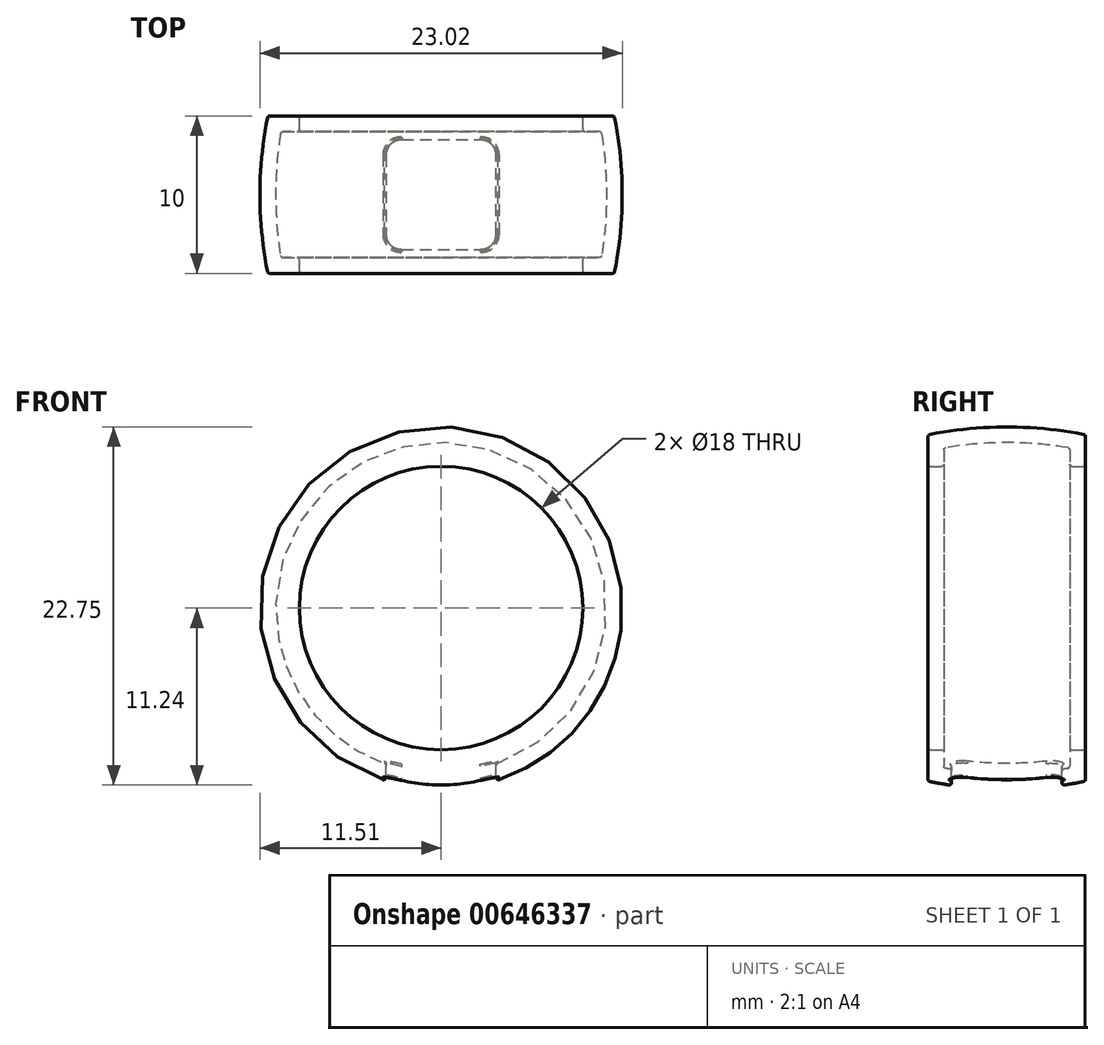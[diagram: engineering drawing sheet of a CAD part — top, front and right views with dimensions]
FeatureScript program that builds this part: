
annotation { "Feature Type Name" : "Feature", "Feature Type Description" : "" }
export const myFeature = defineFeature(function(context is Context, id is Id, definition is map)
    precondition{}
    {
        {
            var Q0;
            Q0=qCreatedBy(makeId("Top.planeOp"),FACE);
            var sketch = newSketch(context, id + "F0", { "sketchPlane" : qUnion([Q0])});
            skLineSegment(sketch, "E0", {"start": v(0, 0) * mm, "end": v(-9, 0) * mm, "construction": true});
            skLineSegment(sketch, "E1", {"start": v(-9, 5) * mm, "end": v(-9, -5) * mm});
            skLineSegment(sketch, "E2", {"start": v(-9, 5) * mm, "end": v(-11, 5) * mm});
            skLineSegment(sketch, "E3", {"start": v(-9, -5) * mm, "end": v(-11, -5) * mm});
            skArc(sketch, "E4", {"start": v(-11, 5) * mm, "mid": v(-11.5, 0) * mm, "end": v(-11, -5) * mm});
            skLineSegment(sketch, "E5", {"start": v(0, 0) * mm, "end": v(0, -13.53) * mm, "construction": true});
            skSolve(sketch);
        }
        {
            var Q0;
            Q0 = qSketchRegion(id + "F0", true);
            var Q1;
            Q1=sQuery(id+"F0.wireOp",EDGE,"E5");
            revolve(context, id + "F1", {"entities" : qUnion([Q0]), "axis" : qUnion([Q1]), "revolveType" : RevolveType.FULL});
        }
        {
            var Q0;
            Q0=makeQuery(id+"F1.opRevolve","SWEPT_FACE",FACE,{"disambiguationData":[OSD([sQuery(id+"F0.wireOp",EDGE,"E1")])]});
            shell(context, id + "F2", {"entities" : qUnion([Q0]), "thickness" : 1 * mm});
        }
        {
            var Q0;
            Q0=makeQuery(id+"F1.opRevolve","SWEPT_FACE",FACE,{"disambiguationData":[OSD([sQuery(id+"F0.wireOp",EDGE,"E4")])]});
            var Q1;
            Q1=makeQuery(id+"F1.opRevolve","SWEPT_EDGE",EDGE,{"disambiguationData":[OSD([sQuery(id+"F0.wireOp",EDGE,"E3"),sQuery(id+"F0.wireOp",EDGE,"E4")])]});
            var Q2;
            Q2=makeQuery(id+"F1.opRevolve","SWEPT_FACE",FACE,{"disambiguationData":[OSD([sQuery(id+"F0.wireOp",EDGE,"E3")])]});
            var Q3;
            Q3=makeQuery(id+"F1.opRevolve","SWEPT_EDGE",EDGE,{"disambiguationData":[OSD([sQuery(id+"F0.wireOp",EDGE,"E2"),sQuery(id+"F0.wireOp",EDGE,"E4")])]});
            var Q4;
            Q4=makeQuery(id+"F1.opRevolve","SWEPT_FACE",FACE,{"disambiguationData":[OSD([sQuery(id+"F0.wireOp",EDGE,"E2")])]});
            var Q5;
            Q5=makeQuery(id+"F1.opRevolve","SWEPT_EDGE",EDGE,{"disambiguationData":[OSD([sQuery(id+"F0.wireOp",EDGE,"E1"),sQuery(id+"F0.wireOp",EDGE,"E3")])]});
            var Q6;
            Q6=makeQuery(id+"F2.opShell","OFFSET_EDGE",EDGE,{"disambiguationData":[OSD([sQuery(id+"F0.wireOp",EDGE,"E1"),sQuery(id+"F0.wireOp",EDGE,"E2")])]});
            var Q7;
            Q7=makeQuery(id+"F1.opRevolve","SWEPT_EDGE",EDGE,{"disambiguationData":[OSD([sQuery(id+"F0.wireOp",EDGE,"E1"),sQuery(id+"F0.wireOp",EDGE,"E2")])]});
            var Q8;
            Q8=makeQuery(id+"F2.opShell","OFFSET_FACE",FACE,{"disambiguationData":[OSD([sQuery(id+"F0.wireOp",EDGE,"E1")])]});
            var Q9;
            Q9=makeQuery(id+"F2.opShell","OFFSET_EDGE",EDGE,{"disambiguationData":[OSD([sQuery(id+"F0.wireOp",EDGE,"E1"),sQuery(id+"F0.wireOp",EDGE,"E3")])]});
            var Q10;
            Q10=makeQuery(id+"F2.opShell","OFFSET_FACE",FACE,{"disambiguationData":[OSD([sQuery(id+"F0.wireOp",EDGE,"E2")])]});
            var Q11;
            Q11=makeQuery(id+"F2.opShell","OFFSET_EDGE",EDGE,{"disambiguationData":[OSD([sQuery(id+"F0.wireOp",EDGE,"E2"),sQuery(id+"F0.wireOp",EDGE,"E4")])]});
            var Q12;
            Q12=makeQuery(id+"F2.opShell","OFFSET_FACE",FACE,{"disambiguationData":[OSD([sQuery(id+"F0.wireOp",EDGE,"E3")])]});
            var Q13;
            Q13=makeQuery(id+"F2.opShell","OFFSET_FACE",FACE,{"disambiguationData":[OSD([sQuery(id+"F0.wireOp",EDGE,"E4")])]});
            var Q14;
            Q14=makeQuery(id+"F1.opRevolve","SWEPT_FACE",FACE,{"disambiguationData":[OSD([sQuery(id+"F0.wireOp",EDGE,"E1")])]});
            var Q15;
            Q15=makeQuery(id+"F2.opShell","OFFSET_EDGE",EDGE,{"disambiguationData":[OSD([sQuery(id+"F0.wireOp",EDGE,"E3"),sQuery(id+"F0.wireOp",EDGE,"E4")])]});
            fillet(context, id + "F3", {"entities" : qUnion([Q0, Q1, Q2, Q3, Q4, Q5, Q6, Q7, Q8, Q9, Q10, Q11, Q12, Q13, Q14, Q15]), "radius" : 0.15 * mm, "tangentPropagation" : true, "allowEdgeOverflow" : false});
        }
        {
            var Q0;
            Q0=qCreatedBy(makeId("Top.planeOp"),FACE);
            var sketch = newSketch(context, id + "F4", { "sketchPlane" : qUnion([Q0])});
            skLineSegment(sketch, "E6.bottom", {"start": v(-2.5, 3.5) * mm, "end": v(2.5, 3.5) * mm});
            skLineSegment(sketch, "E6.top", {"start": v(-2.5, -3.5) * mm, "end": v(2.5, -3.5) * mm});
            skLineSegment(sketch, "E6.left", {"start": v(-3.5, 2.5) * mm, "end": v(-3.5, -2.5) * mm});
            skLineSegment(sketch, "E6.right", {"start": v(3.5, 2.5) * mm, "end": v(3.5, -2.5) * mm});
            skPoint(sketch, "E6.middle", {"position": v(0, 0) * mm});
            skPoint(sketch, "E7.visualSharp", {"position": v(-3.5, 3.5) * mm});
            skArc(sketch, "E7.filletArc", {"start": v(-2.5, 3.5) * mm, "mid": v(-3.2, 3.2) * mm, "end": v(-3.5, 2.5) * mm});
            skPoint(sketch, "E8.visualSharp", {"position": v(3.5, 3.5) * mm});
            skArc(sketch, "E8.filletArc", {"start": v(3.5, 2.5) * mm, "mid": v(3.2, 3.2) * mm, "end": v(2.5, 3.5) * mm});
            skPoint(sketch, "E9.visualSharp", {"position": v(3.5, -3.5) * mm});
            skArc(sketch, "E9.filletArc", {"start": v(2.5, -3.5) * mm, "mid": v(3.2, -3.2) * mm, "end": v(3.5, -2.5) * mm});
            skPoint(sketch, "E10.visualSharp", {"position": v(-3.5, -3.5) * mm});
            skArc(sketch, "E10.filletArc", {"start": v(-3.5, -2.5) * mm, "mid": v(-3.2, -3.2) * mm, "end": v(-2.5, -3.5) * mm});
            skSolve(sketch);
        }
        {
            var Q0;
            Q0 = qSketchRegion(id + "F4", true);
            extrude(context, id + "F5", {"entities" : qUnion([Q0]), "operationType" : NewBodyOperationType.REMOVE, "endBound" : BoundingType.THROUGH_ALL, "oppositeDirection" : true, "depth" : 25 * mm, "offsetDistance" : 25 * mm});
        }
        {
            var Q0;
            {var subQ0=sQuery(id+"F0.wireOp",EDGE,"E3");Q0=makeQuery(id+"F3.opFillet","BLEND_EDGE",EDGE,{"blendedFrom":[makeQuery(id+"F1.opRevolve","SWEPT_EDGE",EDGE,{"disambiguationData":[OSD([sQuery(id+"F0.wireOp",EDGE,"E1"),subQ0])]}),makeQuery(id+"F1.opRevolve","SWEPT_FACE",FACE,{"disambiguationData":[OSD([subQ0])]})],"blendedInto":[makeQuery(id+"F1.opRevolve","SWEPT_FACE",FACE,{"disambiguationData":[OSD([subQ0])]})]});}
            var Q1;
            {var subQ0=sQuery(id+"F0.wireOp",EDGE,"E3");var subQ1=sQuery(id+"F0.wireOp",EDGE,"E1");Q1=makeQuery(id+"F3.opFillet","BLEND_FACE",FACE,{"disambiguationData":[OSD([subQ1,subQ0]),TDD([makeQuery(id+"F1.opRevolve","SWEPT_EDGE",EDGE,{"disambiguationData":[OSD([subQ1,subQ0])]})])]});}
            var Q2;
            {var subQ0=sQuery(id+"F0.wireOp",EDGE,"E1");Q2=makeQuery(id+"F3.opFillet","BLEND_EDGE",EDGE,{"blendedFrom":[makeQuery(id+"F1.opRevolve","SWEPT_EDGE",EDGE,{"disambiguationData":[OSD([subQ0,sQuery(id+"F0.wireOp",EDGE,"E3")])]}),makeQuery(id+"F1.opRevolve","SWEPT_FACE",FACE,{"disambiguationData":[OSD([subQ0])]})],"blendedInto":[makeQuery(id+"F1.opRevolve","SWEPT_FACE",FACE,{"disambiguationData":[OSD([subQ0])]})]});}
            var Q3;
            {var subQ0=sQuery(id+"F0.wireOp",EDGE,"E4");var subQ1=sQuery(id+"F0.wireOp",EDGE,"E2");Q3=makeQuery(id+"F3.opFillet","BLEND_FACE",FACE,{"disambiguationData":[OSD([subQ1,subQ0]),TDD([makeQuery(id+"F1.opRevolve","SWEPT_EDGE",EDGE,{"disambiguationData":[OSD([subQ1,subQ0])]})])]});}
            var Q4;
            {var subQ0=sQuery(id+"F0.wireOp",EDGE,"E2");Q4=makeQuery(id+"F3.opFillet","BLEND_EDGE",EDGE,{"blendedFrom":[makeQuery(id+"F1.opRevolve","SWEPT_EDGE",EDGE,{"disambiguationData":[OSD([subQ0,sQuery(id+"F0.wireOp",EDGE,"E4")])]}),makeQuery(id+"F1.opRevolve","SWEPT_FACE",FACE,{"disambiguationData":[OSD([subQ0])]})],"blendedInto":[makeQuery(id+"F1.opRevolve","SWEPT_FACE",FACE,{"disambiguationData":[OSD([subQ0])]})]});}
            var Q5;
            {var subQ0=sQuery(id+"F0.wireOp",EDGE,"E4");var subQ1=sQuery(id+"F0.wireOp",EDGE,"E3");Q5=makeQuery(id+"F3.opFillet","BLEND_FACE",FACE,{"disambiguationData":[OSD([subQ1,subQ0]),TDD([makeQuery(id+"F1.opRevolve","SWEPT_EDGE",EDGE,{"disambiguationData":[OSD([subQ1,subQ0])]})])]});}
            var Q6;
            {var subQ0=sQuery(id+"F0.wireOp",EDGE,"E1");Q6=makeQuery(id+"F3.opFillet","BLEND_EDGE",EDGE,{"blendedFrom":[makeQuery(id+"F1.opRevolve","SWEPT_EDGE",EDGE,{"disambiguationData":[OSD([subQ0,sQuery(id+"F0.wireOp",EDGE,"E2")])]}),makeQuery(id+"F2.opShell","OFFSET_FACE",FACE,{"disambiguationData":[OSD([subQ0])]})],"blendedInto":[makeQuery(id+"F2.opShell","OFFSET_FACE",FACE,{"disambiguationData":[OSD([subQ0])]})]});}
            var Q7;
            {var subQ0=sQuery(id+"F0.wireOp",EDGE,"E2");var subQ1=sQuery(id+"F0.wireOp",EDGE,"E1");Q7=makeQuery(id+"F3.opFillet","BLEND_FACE",FACE,{"disambiguationData":[OSD([subQ1,subQ0]),TDD([makeQuery(id+"F2.opShell","OFFSET_EDGE",EDGE,{"disambiguationData":[OSD([subQ1,subQ0])]})])]});}
            var Q8;
            {var subQ0=sQuery(id+"F0.wireOp",EDGE,"E2");var subQ1=sQuery(id+"F0.wireOp",EDGE,"E1");Q8=makeQuery(id+"F3.opFillet","BLEND_FACE",FACE,{"disambiguationData":[OSD([subQ1,subQ0]),TDD([makeQuery(id+"F1.opRevolve","SWEPT_EDGE",EDGE,{"disambiguationData":[OSD([subQ1,subQ0])]})])]});}
            var Q9;
            Q9=makeQuery(id+"F2.opShell","OFFSET_FACE",FACE,{"disambiguationData":[OSD([sQuery(id+"F0.wireOp",EDGE,"E3")])]});
            var Q10;
            Q10=makeQuery(id+"F1.opRevolve","SWEPT_FACE",FACE,{"disambiguationData":[OSD([sQuery(id+"F0.wireOp",EDGE,"E1")])]});
            var Q11;
            {var subQ0=sQuery(id+"F0.wireOp",EDGE,"E4");Q11=makeQuery(id+"F3.opFillet","BLEND_EDGE",EDGE,{"blendedFrom":[makeQuery(id+"F1.opRevolve","SWEPT_EDGE",EDGE,{"disambiguationData":[OSD([sQuery(id+"F0.wireOp",EDGE,"E2"),subQ0])]}),makeQuery(id+"F1.opRevolve","SWEPT_FACE",FACE,{"disambiguationData":[OSD([subQ0])]})],"blendedInto":[makeQuery(id+"F1.opRevolve","SWEPT_FACE",FACE,{"disambiguationData":[OSD([subQ0])]})]});}
            var Q12;
            {var subQ0=sQuery(id+"F0.wireOp",EDGE,"E3");var subQ1=sQuery(id+"F0.wireOp",EDGE,"E1");Q12=makeQuery(id+"F3.opFillet","BLEND_FACE",FACE,{"disambiguationData":[OSD([subQ1,subQ0]),TDD([makeQuery(id+"F2.opShell","OFFSET_EDGE",EDGE,{"disambiguationData":[OSD([subQ1,subQ0])]})])]});}
            var Q13;
            {var subQ0=sQuery(id+"F0.wireOp",EDGE,"E3");Q13=makeQuery(id+"F3.opFillet","BLEND_EDGE",EDGE,{"blendedFrom":[makeQuery(id+"F1.opRevolve","SWEPT_EDGE",EDGE,{"disambiguationData":[OSD([subQ0,sQuery(id+"F0.wireOp",EDGE,"E4")])]}),makeQuery(id+"F1.opRevolve","SWEPT_FACE",FACE,{"disambiguationData":[OSD([subQ0])]})],"blendedInto":[makeQuery(id+"F1.opRevolve","SWEPT_FACE",FACE,{"disambiguationData":[OSD([subQ0])]})]});}
            var Q14;
            {var subQ0=sQuery(id+"F0.wireOp",EDGE,"E4");var subQ1=sQuery(id+"F0.wireOp",EDGE,"E2");Q14=makeQuery(id+"F3.opFillet","BLEND_FACE",FACE,{"disambiguationData":[OSD([subQ1,subQ0]),TDD([makeQuery(id+"F2.opShell","OFFSET_EDGE",EDGE,{"disambiguationData":[OSD([subQ1,subQ0])]})])]});}
            var Q15;
            {var subQ0=sQuery(id+"F0.wireOp",EDGE,"E4");Q15=makeQuery(id+"F3.opFillet","BLEND_EDGE",EDGE,{"blendedFrom":[makeQuery(id+"F1.opRevolve","SWEPT_EDGE",EDGE,{"disambiguationData":[OSD([sQuery(id+"F0.wireOp",EDGE,"E3"),subQ0])]}),makeQuery(id+"F1.opRevolve","SWEPT_FACE",FACE,{"disambiguationData":[OSD([subQ0])]})],"blendedInto":[makeQuery(id+"F1.opRevolve","SWEPT_FACE",FACE,{"disambiguationData":[OSD([subQ0])]})]});}
            var Q16;
            Q16=makeQuery(id+"F1.opRevolve","SWEPT_FACE",FACE,{"disambiguationData":[OSD([sQuery(id+"F0.wireOp",EDGE,"E2")])]});
            var Q17;
            Q17=makeQuery(id+"F1.opRevolve","SWEPT_FACE",FACE,{"disambiguationData":[OSD([sQuery(id+"F0.wireOp",EDGE,"E3")])]});
            var Q18;
            {var subQ0=sQuery(id+"F0.wireOp",EDGE,"E1");Q18=makeQuery(id+"F3.opFillet","BLEND_EDGE",EDGE,{"blendedFrom":[makeQuery(id+"F2.opShell","OFFSET_EDGE",EDGE,{"disambiguationData":[OSD([subQ0,sQuery(id+"F0.wireOp",EDGE,"E3")])]}),makeQuery(id+"F1.opRevolve","SWEPT_FACE",FACE,{"disambiguationData":[OSD([subQ0])]})],"blendedInto":[makeQuery(id+"F1.opRevolve","SWEPT_FACE",FACE,{"disambiguationData":[OSD([subQ0])]})]});}
            var Q19;
            Q19=makeQuery(id+"F2.opShell","OFFSET_FACE",FACE,{"disambiguationData":[OSD([sQuery(id+"F0.wireOp",EDGE,"E1")])]});
            var Q20;
            Q20=makeQuery(id+"F2.opShell","OFFSET_FACE",FACE,{"disambiguationData":[OSD([sQuery(id+"F0.wireOp",EDGE,"E2")])]});
            var Q21;
            Q21=makeQuery(id+"F5.boolean.opBoolean","INTERSECT",EDGE,{"derivedFrom":[makeQuery(id+"F1.opRevolve","SWEPT_FACE",FACE,{"disambiguationData":[OSD([sQuery(id+"F0.wireOp",EDGE,"E4")])]}),makeQuery(id+"F5.opExtrude","SWEPT_FACE",FACE,{"disambiguationData":[OSD([sQuery(id+"F4.wireOp",EDGE,"E6.right")])]})]});
            var Q22;
            Q22=makeQuery(id+"F5.boolean.opBoolean","COPY",FACE,{"derivedFrom":makeQuery(id+"F5.opExtrude","SWEPT_FACE",FACE,{"disambiguationData":[OSD([sQuery(id+"F4.wireOp",EDGE,"E6.bottom")])]})});
            var Q23;
            Q23=makeQuery(id+"F5.boolean.opBoolean","COPY",FACE,{"derivedFrom":makeQuery(id+"F5.opExtrude","SWEPT_FACE",FACE,{"disambiguationData":[OSD([sQuery(id+"F4.wireOp",EDGE,"E6.top")])]})});
            var Q24;
            Q24=makeQuery(id+"F5.boolean.opBoolean","COPY",FACE,{"derivedFrom":makeQuery(id+"F5.opExtrude","SWEPT_FACE",FACE,{"disambiguationData":[OSD([sQuery(id+"F4.wireOp",EDGE,"E6.left")])]})});
            var Q25;
            Q25=makeQuery(id+"F5.boolean.opBoolean","COPY",FACE,{"derivedFrom":makeQuery(id+"F5.opExtrude","SWEPT_FACE",FACE,{"disambiguationData":[OSD([sQuery(id+"F4.wireOp",EDGE,"E7.filletArc")])]})});
            var Q26;
            Q26=makeQuery(id+"F5.boolean.opBoolean","COPY",FACE,{"derivedFrom":makeQuery(id+"F5.opExtrude","SWEPT_FACE",FACE,{"disambiguationData":[OSD([sQuery(id+"F4.wireOp",EDGE,"E8.filletArc")])]})});
            var Q27;
            Q27=makeQuery(id+"F5.boolean.opBoolean","INTERSECT",EDGE,{"derivedFrom":[makeQuery(id+"F1.opRevolve","SWEPT_FACE",FACE,{"disambiguationData":[OSD([sQuery(id+"F0.wireOp",EDGE,"E4")])]}),makeQuery(id+"F5.opExtrude","SWEPT_FACE",FACE,{"disambiguationData":[OSD([sQuery(id+"F4.wireOp",EDGE,"E6.bottom")])]})]});
            var Q28;
            Q28=makeQuery(id+"F5.boolean.opBoolean","INTERSECT",EDGE,{"derivedFrom":[makeQuery(id+"F2.opShell","OFFSET_FACE",FACE,{"disambiguationData":[OSD([sQuery(id+"F0.wireOp",EDGE,"E4")])]}),makeQuery(id+"F5.opExtrude","SWEPT_FACE",FACE,{"disambiguationData":[OSD([sQuery(id+"F4.wireOp",EDGE,"E6.bottom")])]})]});
            var Q29;
            Q29=makeQuery(id+"F5.boolean.opBoolean","INTERSECT",EDGE,{"derivedFrom":[makeQuery(id+"F1.opRevolve","SWEPT_FACE",FACE,{"disambiguationData":[OSD([sQuery(id+"F0.wireOp",EDGE,"E4")])]}),makeQuery(id+"F5.opExtrude","SWEPT_FACE",FACE,{"disambiguationData":[OSD([sQuery(id+"F4.wireOp",EDGE,"E6.top")])]})]});
            var Q30;
            Q30=makeQuery(id+"F5.boolean.opBoolean","INTERSECT",EDGE,{"derivedFrom":[makeQuery(id+"F1.opRevolve","SWEPT_FACE",FACE,{"disambiguationData":[OSD([sQuery(id+"F0.wireOp",EDGE,"E4")])]}),makeQuery(id+"F5.opExtrude","SWEPT_FACE",FACE,{"disambiguationData":[OSD([sQuery(id+"F4.wireOp",EDGE,"E6.left")])]})]});
            var Q31;
            Q31=makeQuery(id+"F5.boolean.opBoolean","INTERSECT",EDGE,{"derivedFrom":[makeQuery(id+"F1.opRevolve","SWEPT_FACE",FACE,{"disambiguationData":[OSD([sQuery(id+"F0.wireOp",EDGE,"E4")])]}),makeQuery(id+"F5.opExtrude","SWEPT_FACE",FACE,{"disambiguationData":[OSD([sQuery(id+"F4.wireOp",EDGE,"E10.filletArc")])]})]});
            var Q32;
            Q32=makeQuery(id+"FnJFpvDc8nEjpgP_1.1.F5.boolean.opBoolean","INTERSECT",EDGE,{"derivedFrom":[makeQuery(id+"F1.opRevolve","SWEPT_FACE",FACE,{"disambiguationData":[OSD([sQuery(id+"F0.wireOp",EDGE,"E4")])]}),makeQuery(id+"FnJFpvDc8nEjpgP_1.1.F5.opExtrude","SWEPT_FACE",FACE,{"disambiguationData":[OSD([sQuery(id+"F4.wireOp",EDGE,"E6.right")])]})]});
            var Q33;
            Q33=makeQuery(id+"FnJFpvDc8nEjpgP_1.1.F5.boolean.opBoolean","INTERSECT",EDGE,{"derivedFrom":[makeQuery(id+"F2.opShell","OFFSET_FACE",FACE,{"disambiguationData":[OSD([sQuery(id+"F0.wireOp",EDGE,"E4")])]}),makeQuery(id+"FnJFpvDc8nEjpgP_1.1.F5.opExtrude","SWEPT_FACE",FACE,{"disambiguationData":[OSD([sQuery(id+"F4.wireOp",EDGE,"E6.right")])]})]});
            var Q34;
            Q34=makeQuery(id+"FnJFpvDc8nEjpgP_1.1.F5.boolean.opBoolean","COPY",FACE,{"derivedFrom":makeQuery(id+"FnJFpvDc8nEjpgP_1.1.F5.opExtrude","SWEPT_FACE",FACE,{"disambiguationData":[OSD([sQuery(id+"F4.wireOp",EDGE,"E6.bottom")])]})});
            var Q35;
            Q35=makeQuery(id+"FnJFpvDc8nEjpgP_1.1.F5.boolean.opBoolean","COPY",FACE,{"derivedFrom":makeQuery(id+"FnJFpvDc8nEjpgP_1.1.F5.opExtrude","SWEPT_FACE",FACE,{"disambiguationData":[OSD([sQuery(id+"F4.wireOp",EDGE,"E6.top")])]})});
            var Q36;
            Q36=makeQuery(id+"FnJFpvDc8nEjpgP_1.1.F5.boolean.opBoolean","COPY",FACE,{"derivedFrom":makeQuery(id+"FnJFpvDc8nEjpgP_1.1.F5.opExtrude","SWEPT_FACE",FACE,{"disambiguationData":[OSD([sQuery(id+"F4.wireOp",EDGE,"E6.right")])]})});
            var Q37;
            Q37=makeQuery(id+"FnJFpvDc8nEjpgP_1.1.F5.boolean.opBoolean","COPY",FACE,{"derivedFrom":makeQuery(id+"FnJFpvDc8nEjpgP_1.1.F5.opExtrude","SWEPT_FACE",FACE,{"disambiguationData":[OSD([sQuery(id+"F4.wireOp",EDGE,"E8.filletArc")])]})});
            var Q38;
            Q38=makeQuery(id+"FnJFpvDc8nEjpgP_1.1.F5.boolean.opBoolean","COPY",FACE,{"derivedFrom":makeQuery(id+"FnJFpvDc8nEjpgP_1.1.F5.opExtrude","SWEPT_FACE",FACE,{"disambiguationData":[OSD([sQuery(id+"F4.wireOp",EDGE,"E10.filletArc")])]})});
            var Q39;
            Q39=makeQuery(id+"FnJFpvDc8nEjpgP_1.1.F5.boolean.opBoolean","INTERSECT",EDGE,{"derivedFrom":[makeQuery(id+"F1.opRevolve","SWEPT_FACE",FACE,{"disambiguationData":[OSD([sQuery(id+"F0.wireOp",EDGE,"E4")])]}),makeQuery(id+"FnJFpvDc8nEjpgP_1.1.F5.opExtrude","SWEPT_FACE",FACE,{"disambiguationData":[OSD([sQuery(id+"F4.wireOp",EDGE,"E6.bottom")])]})]});
            var Q40;
            Q40=makeQuery(id+"FnJFpvDc8nEjpgP_1.1.F5.boolean.opBoolean","INTERSECT",EDGE,{"derivedFrom":[makeQuery(id+"F2.opShell","OFFSET_FACE",FACE,{"disambiguationData":[OSD([sQuery(id+"F0.wireOp",EDGE,"E4")])]}),makeQuery(id+"FnJFpvDc8nEjpgP_1.1.F5.opExtrude","SWEPT_FACE",FACE,{"disambiguationData":[OSD([sQuery(id+"F4.wireOp",EDGE,"E6.bottom")])]})]});
            var Q41;
            Q41=makeQuery(id+"FnJFpvDc8nEjpgP_1.1.F5.boolean.opBoolean","INTERSECT",EDGE,{"derivedFrom":[makeQuery(id+"F1.opRevolve","SWEPT_FACE",FACE,{"disambiguationData":[OSD([sQuery(id+"F0.wireOp",EDGE,"E4")])]}),makeQuery(id+"FnJFpvDc8nEjpgP_1.1.F5.opExtrude","SWEPT_FACE",FACE,{"disambiguationData":[OSD([sQuery(id+"F4.wireOp",EDGE,"E6.top")])]})]});
            var Q42;
            Q42=makeQuery(id+"FnJFpvDc8nEjpgP_1.1.F5.boolean.opBoolean","INTERSECT",EDGE,{"derivedFrom":[makeQuery(id+"F1.opRevolve","SWEPT_FACE",FACE,{"disambiguationData":[OSD([sQuery(id+"F0.wireOp",EDGE,"E4")])]}),makeQuery(id+"FnJFpvDc8nEjpgP_1.1.F5.opExtrude","SWEPT_FACE",FACE,{"disambiguationData":[OSD([sQuery(id+"F4.wireOp",EDGE,"E6.left")])]})]});
            var Q43;
            Q43=makeQuery(id+"FnJFpvDc8nEjpgP_1.2.F5.boolean.opBoolean","COPY",FACE,{"derivedFrom":makeQuery(id+"FnJFpvDc8nEjpgP_1.2.F5.opExtrude","SWEPT_FACE",FACE,{"disambiguationData":[OSD([sQuery(id+"F4.wireOp",EDGE,"E6.left")])]})});
            var Q44;
            Q44=makeQuery(id+"FnJFpvDc8nEjpgP_1.2.F5.boolean.opBoolean","INTERSECT",EDGE,{"derivedFrom":[makeQuery(id+"F1.opRevolve","SWEPT_FACE",FACE,{"disambiguationData":[OSD([sQuery(id+"F0.wireOp",EDGE,"E4")])]}),makeQuery(id+"FnJFpvDc8nEjpgP_1.2.F5.opExtrude","SWEPT_FACE",FACE,{"disambiguationData":[OSD([sQuery(id+"F4.wireOp",EDGE,"E6.left")])]})]});
            var Q45;
            Q45=makeQuery(id+"FnJFpvDc8nEjpgP_1.3.F5.boolean.opBoolean","INTERSECT",EDGE,{"derivedFrom":[makeQuery(id+"F1.opRevolve","SWEPT_FACE",FACE,{"disambiguationData":[OSD([sQuery(id+"F0.wireOp",EDGE,"E4")])]}),makeQuery(id+"FnJFpvDc8nEjpgP_1.3.F5.opExtrude","SWEPT_FACE",FACE,{"disambiguationData":[OSD([sQuery(id+"F4.wireOp",EDGE,"E6.right")])]})]});
            var Q46;
            Q46=makeQuery(id+"FnJFpvDc8nEjpgP_1.3.F5.boolean.opBoolean","COPY",FACE,{"derivedFrom":makeQuery(id+"FnJFpvDc8nEjpgP_1.3.F5.opExtrude","SWEPT_FACE",FACE,{"disambiguationData":[OSD([sQuery(id+"F4.wireOp",EDGE,"E6.bottom")])]})});
            var Q47;
            Q47=makeQuery(id+"FnJFpvDc8nEjpgP_1.3.F5.boolean.opBoolean","COPY",FACE,{"derivedFrom":makeQuery(id+"FnJFpvDc8nEjpgP_1.3.F5.opExtrude","SWEPT_FACE",FACE,{"disambiguationData":[OSD([sQuery(id+"F4.wireOp",EDGE,"E6.right")])]})});
            var Q48;
            Q48=makeQuery(id+"FnJFpvDc8nEjpgP_1.4.F5.boolean.opBoolean","INTERSECT",EDGE,{"derivedFrom":[makeQuery(id+"F2.opShell","OFFSET_FACE",FACE,{"disambiguationData":[OSD([sQuery(id+"F0.wireOp",EDGE,"E4")])]}),makeQuery(id+"FnJFpvDc8nEjpgP_1.4.F5.opExtrude","SWEPT_FACE",FACE,{"disambiguationData":[OSD([sQuery(id+"F4.wireOp",EDGE,"E6.right")])]})]});
            var Q49;
            Q49=makeQuery(id+"FnJFpvDc8nEjpgP_1.4.F5.boolean.opBoolean","COPY",FACE,{"derivedFrom":makeQuery(id+"FnJFpvDc8nEjpgP_1.4.F5.opExtrude","SWEPT_FACE",FACE,{"disambiguationData":[OSD([sQuery(id+"F4.wireOp",EDGE,"E6.left")])]})});
            var Q50;
            Q50=makeQuery(id+"FnJFpvDc8nEjpgP_1.4.F5.boolean.opBoolean","COPY",FACE,{"derivedFrom":makeQuery(id+"FnJFpvDc8nEjpgP_1.4.F5.opExtrude","SWEPT_FACE",FACE,{"disambiguationData":[OSD([sQuery(id+"F4.wireOp",EDGE,"E9.filletArc")])]})});
            var Q51;
            Q51=makeQuery(id+"FnJFpvDc8nEjpgP_1.4.F5.boolean.opBoolean","COPY",FACE,{"derivedFrom":makeQuery(id+"FnJFpvDc8nEjpgP_1.4.F5.opExtrude","SWEPT_FACE",FACE,{"disambiguationData":[OSD([sQuery(id+"F4.wireOp",EDGE,"E10.filletArc")])]})});
            var Q52;
            Q52=makeQuery(id+"FnJFpvDc8nEjpgP_1.5.F5.boolean.opBoolean","INTERSECT",EDGE,{"derivedFrom":[makeQuery(id+"F2.opShell","OFFSET_FACE",FACE,{"disambiguationData":[OSD([sQuery(id+"F0.wireOp",EDGE,"E4")])]}),makeQuery(id+"FnJFpvDc8nEjpgP_1.5.F5.opExtrude","SWEPT_FACE",FACE,{"disambiguationData":[OSD([sQuery(id+"F4.wireOp",EDGE,"E6.left")])]})]});
            var Q53;
            Q53=makeQuery(id+"FnJFpvDc8nEjpgP_1.5.F5.boolean.opBoolean","COPY",FACE,{"derivedFrom":makeQuery(id+"FnJFpvDc8nEjpgP_1.5.F5.opExtrude","SWEPT_FACE",FACE,{"disambiguationData":[OSD([sQuery(id+"F4.wireOp",EDGE,"E6.left")])]})});
            var Q54;
            Q54=makeQuery(id+"FnJFpvDc8nEjpgP_1.6.F5.boolean.opBoolean","INTERSECT",EDGE,{"derivedFrom":[makeQuery(id+"F2.opShell","OFFSET_FACE",FACE,{"disambiguationData":[OSD([sQuery(id+"F0.wireOp",EDGE,"E4")])]}),makeQuery(id+"FnJFpvDc8nEjpgP_1.6.F5.opExtrude","SWEPT_FACE",FACE,{"disambiguationData":[OSD([sQuery(id+"F4.wireOp",EDGE,"E6.left")])]})]});
            var Q55;
            Q55=makeQuery(id+"FnJFpvDc8nEjpgP_1.6.F5.boolean.opBoolean","INTERSECT",EDGE,{"derivedFrom":[makeQuery(id+"F1.opRevolve","SWEPT_FACE",FACE,{"disambiguationData":[OSD([sQuery(id+"F0.wireOp",EDGE,"E4")])]}),makeQuery(id+"FnJFpvDc8nEjpgP_1.6.F5.opExtrude","SWEPT_FACE",FACE,{"disambiguationData":[OSD([sQuery(id+"F4.wireOp",EDGE,"E6.right")])]})]});
            var Q56;
            Q56=makeQuery(id+"FnJFpvDc8nEjpgP_1.6.F5.boolean.opBoolean","COPY",FACE,{"derivedFrom":makeQuery(id+"FnJFpvDc8nEjpgP_1.6.F5.opExtrude","SWEPT_FACE",FACE,{"disambiguationData":[OSD([sQuery(id+"F4.wireOp",EDGE,"E6.bottom")])]})});
            var Q57;
            Q57=makeQuery(id+"FnJFpvDc8nEjpgP_1.6.F5.boolean.opBoolean","COPY",FACE,{"derivedFrom":makeQuery(id+"FnJFpvDc8nEjpgP_1.6.F5.opExtrude","SWEPT_FACE",FACE,{"disambiguationData":[OSD([sQuery(id+"F4.wireOp",EDGE,"E6.left")])]})});
            var Q58;
            Q58=makeQuery(id+"FnJFpvDc8nEjpgP_1.6.F5.boolean.opBoolean","COPY",FACE,{"derivedFrom":makeQuery(id+"FnJFpvDc8nEjpgP_1.6.F5.opExtrude","SWEPT_FACE",FACE,{"disambiguationData":[OSD([sQuery(id+"F4.wireOp",EDGE,"E9.filletArc")])]})});
            var Q59;
            Q59=makeQuery(id+"FnJFpvDc8nEjpgP_1.6.F5.boolean.opBoolean","INTERSECT",EDGE,{"derivedFrom":[makeQuery(id+"F1.opRevolve","SWEPT_FACE",FACE,{"disambiguationData":[OSD([sQuery(id+"F0.wireOp",EDGE,"E4")])]}),makeQuery(id+"FnJFpvDc8nEjpgP_1.6.F5.opExtrude","SWEPT_FACE",FACE,{"disambiguationData":[OSD([sQuery(id+"F4.wireOp",EDGE,"E6.bottom")])]})]});
            var Q60;
            Q60=makeQuery(id+"F1.opRevolve","SWEPT_FACE",FACE,{"disambiguationData":[OSD([sQuery(id+"F0.wireOp",EDGE,"E4")])]});
            var Q61;
            Q61=makeQuery(id+"F2.opShell","OFFSET_FACE",FACE,{"disambiguationData":[OSD([sQuery(id+"F0.wireOp",EDGE,"E4")])]});
            var Q62;
            Q62=makeQuery(id+"FnJFpvDc8nEjpgP_1.6.F5.boolean.opBoolean","INTERSECT",EDGE,{"derivedFrom":[makeQuery(id+"F1.opRevolve","SWEPT_FACE",FACE,{"disambiguationData":[OSD([sQuery(id+"F0.wireOp",EDGE,"E4")])]}),makeQuery(id+"FnJFpvDc8nEjpgP_1.6.F5.opExtrude","SWEPT_FACE",FACE,{"disambiguationData":[OSD([sQuery(id+"F4.wireOp",EDGE,"E6.top")])]})]});
            var Q63;
            Q63=makeQuery(id+"FnJFpvDc8nEjpgP_1.1.F5.boolean.opBoolean","INTERSECT",EDGE,{"derivedFrom":[makeQuery(id+"F1.opRevolve","SWEPT_FACE",FACE,{"disambiguationData":[OSD([sQuery(id+"F0.wireOp",EDGE,"E4")])]}),makeQuery(id+"FnJFpvDc8nEjpgP_1.1.F5.opExtrude","SWEPT_FACE",FACE,{"disambiguationData":[OSD([sQuery(id+"F4.wireOp",EDGE,"E7.filletArc")])]})]});
            var Q64;
            Q64=makeQuery(id+"FnJFpvDc8nEjpgP_1.1.F5.boolean.opBoolean","INTERSECT",EDGE,{"derivedFrom":[makeQuery(id+"F1.opRevolve","SWEPT_FACE",FACE,{"disambiguationData":[OSD([sQuery(id+"F0.wireOp",EDGE,"E4")])]}),makeQuery(id+"FnJFpvDc8nEjpgP_1.1.F5.opExtrude","SWEPT_FACE",FACE,{"disambiguationData":[OSD([sQuery(id+"F4.wireOp",EDGE,"E10.filletArc")])]})]});
            var Q65;
            Q65=makeQuery(id+"FnJFpvDc8nEjpgP_1.4.F5.boolean.opBoolean","INTERSECT",EDGE,{"derivedFrom":[makeQuery(id+"F2.opShell","OFFSET_FACE",FACE,{"disambiguationData":[OSD([sQuery(id+"F0.wireOp",EDGE,"E4")])]}),makeQuery(id+"FnJFpvDc8nEjpgP_1.4.F5.opExtrude","SWEPT_FACE",FACE,{"disambiguationData":[OSD([sQuery(id+"F4.wireOp",EDGE,"E10.filletArc")])]})]});
            var Q66;
            {var subQ0=sQuery(id+"F0.wireOp",EDGE,"E2");Q66=makeQuery(id+"F3.opFillet","BLEND_EDGE",EDGE,{"blendedFrom":[makeQuery(id+"F1.opRevolve","SWEPT_EDGE",EDGE,{"disambiguationData":[OSD([sQuery(id+"F0.wireOp",EDGE,"E1"),subQ0])]}),makeQuery(id+"F1.opRevolve","SWEPT_FACE",FACE,{"disambiguationData":[OSD([subQ0])]})],"blendedInto":[makeQuery(id+"F1.opRevolve","SWEPT_FACE",FACE,{"disambiguationData":[OSD([subQ0])]})]});}
            var Q67;
            {var subQ0=sQuery(id+"F0.wireOp",EDGE,"E4");Q67=makeQuery(id+"F3.opFillet","BLEND_EDGE",EDGE,{"blendedFrom":[makeQuery(id+"F2.opShell","OFFSET_EDGE",EDGE,{"disambiguationData":[OSD([sQuery(id+"F0.wireOp",EDGE,"E3"),subQ0])]}),makeQuery(id+"F2.opShell","OFFSET_FACE",FACE,{"disambiguationData":[OSD([subQ0])]})],"blendedInto":[makeQuery(id+"F2.opShell","OFFSET_FACE",FACE,{"disambiguationData":[OSD([subQ0])]})]});}
            var Q68;
            {var subQ0=sQuery(id+"F0.wireOp",EDGE,"E3");Q68=makeQuery(id+"F3.opFillet","BLEND_EDGE",EDGE,{"blendedFrom":[makeQuery(id+"F2.opShell","OFFSET_EDGE",EDGE,{"disambiguationData":[OSD([subQ0,sQuery(id+"F0.wireOp",EDGE,"E4")])]}),makeQuery(id+"F2.opShell","OFFSET_FACE",FACE,{"disambiguationData":[OSD([subQ0])]})],"blendedInto":[makeQuery(id+"F2.opShell","OFFSET_FACE",FACE,{"disambiguationData":[OSD([subQ0])]})]});}
            var Q69;
            {var subQ0=sQuery(id+"F0.wireOp",EDGE,"E4");Q69=makeQuery(id+"F3.opFillet","BLEND_EDGE",EDGE,{"blendedFrom":[makeQuery(id+"F2.opShell","OFFSET_EDGE",EDGE,{"disambiguationData":[OSD([sQuery(id+"F0.wireOp",EDGE,"E2"),subQ0])]}),makeQuery(id+"F2.opShell","OFFSET_FACE",FACE,{"disambiguationData":[OSD([subQ0])]})],"blendedInto":[makeQuery(id+"F2.opShell","OFFSET_FACE",FACE,{"disambiguationData":[OSD([subQ0])]})]});}
            var Q70;
            {var subQ0=sQuery(id+"F0.wireOp",EDGE,"E4");var subQ1=sQuery(id+"F0.wireOp",EDGE,"E3");Q70=makeQuery(id+"F3.opFillet","BLEND_FACE",FACE,{"disambiguationData":[OSD([subQ1,subQ0]),TDD([makeQuery(id+"F2.opShell","OFFSET_EDGE",EDGE,{"disambiguationData":[OSD([subQ1,subQ0])]})])]});}
            var Q71;
            {var subQ0=sQuery(id+"F0.wireOp",EDGE,"E1");Q71=makeQuery(id+"F3.opFillet","BLEND_EDGE",EDGE,{"blendedFrom":[makeQuery(id+"F2.opShell","OFFSET_EDGE",EDGE,{"disambiguationData":[OSD([subQ0,sQuery(id+"F0.wireOp",EDGE,"E2")])]}),makeQuery(id+"F2.opShell","OFFSET_FACE",FACE,{"disambiguationData":[OSD([subQ0])]})],"blendedInto":[makeQuery(id+"F2.opShell","OFFSET_FACE",FACE,{"disambiguationData":[OSD([subQ0])]})]});}
            var Q72;
            {var subQ0=sQuery(id+"F0.wireOp",EDGE,"E2");Q72=makeQuery(id+"F3.opFillet","BLEND_EDGE",EDGE,{"blendedFrom":[makeQuery(id+"F2.opShell","OFFSET_EDGE",EDGE,{"disambiguationData":[OSD([sQuery(id+"F0.wireOp",EDGE,"E1"),subQ0])]}),makeQuery(id+"F2.opShell","OFFSET_FACE",FACE,{"disambiguationData":[OSD([subQ0])]})],"blendedInto":[makeQuery(id+"F2.opShell","OFFSET_FACE",FACE,{"disambiguationData":[OSD([subQ0])]})]});}
            var Q73;
            {var subQ0=sQuery(id+"F0.wireOp",EDGE,"E3");Q73=makeQuery(id+"F3.opFillet","BLEND_EDGE",EDGE,{"blendedFrom":[makeQuery(id+"F2.opShell","OFFSET_EDGE",EDGE,{"disambiguationData":[OSD([sQuery(id+"F0.wireOp",EDGE,"E1"),subQ0])]}),makeQuery(id+"F2.opShell","OFFSET_FACE",FACE,{"disambiguationData":[OSD([subQ0])]})],"blendedInto":[makeQuery(id+"F2.opShell","OFFSET_FACE",FACE,{"disambiguationData":[OSD([subQ0])]})]});}
            var Q74;
            {var subQ0=sQuery(id+"F0.wireOp",EDGE,"E2");Q74=makeQuery(id+"F3.opFillet","BLEND_EDGE",EDGE,{"blendedFrom":[makeQuery(id+"F2.opShell","OFFSET_EDGE",EDGE,{"disambiguationData":[OSD([subQ0,sQuery(id+"F0.wireOp",EDGE,"E4")])]}),makeQuery(id+"F2.opShell","OFFSET_FACE",FACE,{"disambiguationData":[OSD([subQ0])]})],"blendedInto":[makeQuery(id+"F2.opShell","OFFSET_FACE",FACE,{"disambiguationData":[OSD([subQ0])]})]});}
            var Q75;
            Q75=makeQuery(id+"F5.boolean.opBoolean","INTERSECT",EDGE,{"derivedFrom":[makeQuery(id+"F2.opShell","OFFSET_FACE",FACE,{"disambiguationData":[OSD([sQuery(id+"F0.wireOp",EDGE,"E4")])]}),makeQuery(id+"F5.opExtrude","SWEPT_FACE",FACE,{"disambiguationData":[OSD([sQuery(id+"F4.wireOp",EDGE,"E6.left")])]})]});
            var Q76;
            Q76=makeQuery(id+"F5.boolean.opBoolean","INTERSECT",EDGE,{"derivedFrom":[makeQuery(id+"F2.opShell","OFFSET_FACE",FACE,{"disambiguationData":[OSD([sQuery(id+"F0.wireOp",EDGE,"E4")])]}),makeQuery(id+"F5.opExtrude","SWEPT_FACE",FACE,{"disambiguationData":[OSD([sQuery(id+"F4.wireOp",EDGE,"E6.right")])]})]});
            var Q77;
            Q77=makeQuery(id+"F5.boolean.opBoolean","COPY",EDGE,{"derivedFrom":makeQuery(id+"F5.opExtrude","SWEPT_EDGE",EDGE,{"disambiguationData":[OSD([sQuery(id+"F4.wireOp",EDGE,"E6.bottom"),sQuery(id+"F4.wireOp",EDGE,"E7.filletArc")])]})});
            var Q78;
            Q78=makeQuery(id+"F5.boolean.opBoolean","COPY",EDGE,{"derivedFrom":makeQuery(id+"F5.opExtrude","SWEPT_EDGE",EDGE,{"disambiguationData":[OSD([sQuery(id+"F4.wireOp",EDGE,"E6.top"),sQuery(id+"F4.wireOp",EDGE,"E10.filletArc")])]})});
            var Q79;
            Q79=makeQuery(id+"F5.boolean.opBoolean","COPY",FACE,{"derivedFrom":makeQuery(id+"F5.opExtrude","SWEPT_FACE",FACE,{"disambiguationData":[OSD([sQuery(id+"F4.wireOp",EDGE,"E6.right")])]})});
            var Q80;
            Q80=makeQuery(id+"F5.boolean.opBoolean","COPY",EDGE,{"derivedFrom":makeQuery(id+"F5.opExtrude","SWEPT_EDGE",EDGE,{"disambiguationData":[OSD([sQuery(id+"F4.wireOp",EDGE,"E6.left"),sQuery(id+"F4.wireOp",EDGE,"E7.filletArc")])]})});
            var Q81;
            Q81=makeQuery(id+"F5.boolean.opBoolean","COPY",EDGE,{"derivedFrom":makeQuery(id+"F5.opExtrude","SWEPT_EDGE",EDGE,{"disambiguationData":[OSD([sQuery(id+"F4.wireOp",EDGE,"E6.right"),sQuery(id+"F4.wireOp",EDGE,"E8.filletArc")])]})});
            var Q82;
            Q82=makeQuery(id+"F5.boolean.opBoolean","COPY",FACE,{"derivedFrom":makeQuery(id+"F5.opExtrude","SWEPT_FACE",FACE,{"disambiguationData":[OSD([sQuery(id+"F4.wireOp",EDGE,"E9.filletArc")])]})});
            var Q83;
            Q83=makeQuery(id+"F5.boolean.opBoolean","COPY",FACE,{"derivedFrom":makeQuery(id+"F5.opExtrude","SWEPT_FACE",FACE,{"disambiguationData":[OSD([sQuery(id+"F4.wireOp",EDGE,"E10.filletArc")])]})});
            var Q84;
            Q84=makeQuery(id+"F5.boolean.opBoolean","INTERSECT",EDGE,{"derivedFrom":[makeQuery(id+"F2.opShell","OFFSET_FACE",FACE,{"disambiguationData":[OSD([sQuery(id+"F0.wireOp",EDGE,"E4")])]}),makeQuery(id+"F5.opExtrude","SWEPT_FACE",FACE,{"disambiguationData":[OSD([sQuery(id+"F4.wireOp",EDGE,"E6.top")])]})]});
            var Q85;
            Q85=makeQuery(id+"F5.boolean.opBoolean","INTERSECT",EDGE,{"derivedFrom":[makeQuery(id+"F1.opRevolve","SWEPT_FACE",FACE,{"disambiguationData":[OSD([sQuery(id+"F0.wireOp",EDGE,"E4")])]}),makeQuery(id+"F5.opExtrude","SWEPT_FACE",FACE,{"disambiguationData":[OSD([sQuery(id+"F4.wireOp",EDGE,"E7.filletArc")])]})]});
            var Q86;
            Q86=makeQuery(id+"F5.boolean.opBoolean","INTERSECT",EDGE,{"derivedFrom":[makeQuery(id+"F2.opShell","OFFSET_FACE",FACE,{"disambiguationData":[OSD([sQuery(id+"F0.wireOp",EDGE,"E4")])]}),makeQuery(id+"F5.opExtrude","SWEPT_FACE",FACE,{"disambiguationData":[OSD([sQuery(id+"F4.wireOp",EDGE,"E7.filletArc")])]})]});
            var Q87;
            Q87=makeQuery(id+"F5.boolean.opBoolean","INTERSECT",EDGE,{"derivedFrom":[makeQuery(id+"F1.opRevolve","SWEPT_FACE",FACE,{"disambiguationData":[OSD([sQuery(id+"F0.wireOp",EDGE,"E4")])]}),makeQuery(id+"F5.opExtrude","SWEPT_FACE",FACE,{"disambiguationData":[OSD([sQuery(id+"F4.wireOp",EDGE,"E8.filletArc")])]})]});
            var Q88;
            Q88=makeQuery(id+"F5.boolean.opBoolean","INTERSECT",EDGE,{"derivedFrom":[makeQuery(id+"F2.opShell","OFFSET_FACE",FACE,{"disambiguationData":[OSD([sQuery(id+"F0.wireOp",EDGE,"E4")])]}),makeQuery(id+"F5.opExtrude","SWEPT_FACE",FACE,{"disambiguationData":[OSD([sQuery(id+"F4.wireOp",EDGE,"E8.filletArc")])]})]});
            var Q89;
            Q89=makeQuery(id+"F5.boolean.opBoolean","INTERSECT",EDGE,{"derivedFrom":[makeQuery(id+"F2.opShell","OFFSET_FACE",FACE,{"disambiguationData":[OSD([sQuery(id+"F0.wireOp",EDGE,"E4")])]}),makeQuery(id+"F5.opExtrude","SWEPT_FACE",FACE,{"disambiguationData":[OSD([sQuery(id+"F4.wireOp",EDGE,"E9.filletArc")])]})]});
            var Q90;
            Q90=makeQuery(id+"FnJFpvDc8nEjpgP_1.1.F5.boolean.opBoolean","INTERSECT",EDGE,{"derivedFrom":[makeQuery(id+"F2.opShell","OFFSET_FACE",FACE,{"disambiguationData":[OSD([sQuery(id+"F0.wireOp",EDGE,"E4")])]}),makeQuery(id+"FnJFpvDc8nEjpgP_1.1.F5.opExtrude","SWEPT_FACE",FACE,{"disambiguationData":[OSD([sQuery(id+"F4.wireOp",EDGE,"E6.left")])]})]});
            var Q91;
            Q91=makeQuery(id+"FnJFpvDc8nEjpgP_1.1.F5.boolean.opBoolean","COPY",EDGE,{"derivedFrom":makeQuery(id+"FnJFpvDc8nEjpgP_1.1.F5.opExtrude","SWEPT_EDGE",EDGE,{"disambiguationData":[OSD([sQuery(id+"F4.wireOp",EDGE,"E6.bottom"),sQuery(id+"F4.wireOp",EDGE,"E7.filletArc")])]})});
            var Q92;
            Q92=makeQuery(id+"FnJFpvDc8nEjpgP_1.1.F5.boolean.opBoolean","COPY",EDGE,{"derivedFrom":makeQuery(id+"FnJFpvDc8nEjpgP_1.1.F5.opExtrude","SWEPT_EDGE",EDGE,{"disambiguationData":[OSD([sQuery(id+"F4.wireOp",EDGE,"E6.bottom"),sQuery(id+"F4.wireOp",EDGE,"E8.filletArc")])]})});
            var Q93;
            Q93=makeQuery(id+"FnJFpvDc8nEjpgP_1.1.F5.boolean.opBoolean","COPY",EDGE,{"derivedFrom":makeQuery(id+"FnJFpvDc8nEjpgP_1.1.F5.opExtrude","SWEPT_EDGE",EDGE,{"disambiguationData":[OSD([sQuery(id+"F4.wireOp",EDGE,"E6.top"),sQuery(id+"F4.wireOp",EDGE,"E10.filletArc")])]})});
            var Q94;
            Q94=makeQuery(id+"FnJFpvDc8nEjpgP_1.1.F5.boolean.opBoolean","COPY",FACE,{"derivedFrom":makeQuery(id+"FnJFpvDc8nEjpgP_1.1.F5.opExtrude","SWEPT_FACE",FACE,{"disambiguationData":[OSD([sQuery(id+"F4.wireOp",EDGE,"E6.left")])]})});
            var Q95;
            Q95=makeQuery(id+"FnJFpvDc8nEjpgP_1.1.F5.boolean.opBoolean","COPY",EDGE,{"derivedFrom":makeQuery(id+"FnJFpvDc8nEjpgP_1.1.F5.opExtrude","SWEPT_EDGE",EDGE,{"disambiguationData":[OSD([sQuery(id+"F4.wireOp",EDGE,"E6.top"),sQuery(id+"F4.wireOp",EDGE,"E9.filletArc")])]})});
            var Q96;
            Q96=makeQuery(id+"FnJFpvDc8nEjpgP_1.1.F5.boolean.opBoolean","COPY",EDGE,{"derivedFrom":makeQuery(id+"FnJFpvDc8nEjpgP_1.1.F5.opExtrude","SWEPT_EDGE",EDGE,{"disambiguationData":[OSD([sQuery(id+"F4.wireOp",EDGE,"E6.left"),sQuery(id+"F4.wireOp",EDGE,"E7.filletArc")])]})});
            var Q97;
            Q97=makeQuery(id+"FnJFpvDc8nEjpgP_1.1.F5.boolean.opBoolean","COPY",FACE,{"derivedFrom":makeQuery(id+"FnJFpvDc8nEjpgP_1.1.F5.opExtrude","SWEPT_FACE",FACE,{"disambiguationData":[OSD([sQuery(id+"F4.wireOp",EDGE,"E7.filletArc")])]})});
            var Q98;
            Q98=makeQuery(id+"FnJFpvDc8nEjpgP_1.1.F5.boolean.opBoolean","COPY",EDGE,{"derivedFrom":makeQuery(id+"FnJFpvDc8nEjpgP_1.1.F5.opExtrude","SWEPT_EDGE",EDGE,{"disambiguationData":[OSD([sQuery(id+"F4.wireOp",EDGE,"E6.right"),sQuery(id+"F4.wireOp",EDGE,"E8.filletArc")])]})});
            var Q99;
            Q99=makeQuery(id+"FnJFpvDc8nEjpgP_1.1.F5.boolean.opBoolean","COPY",FACE,{"derivedFrom":makeQuery(id+"FnJFpvDc8nEjpgP_1.1.F5.opExtrude","SWEPT_FACE",FACE,{"disambiguationData":[OSD([sQuery(id+"F4.wireOp",EDGE,"E9.filletArc")])]})});
            var Q100;
            Q100=makeQuery(id+"FnJFpvDc8nEjpgP_1.1.F5.boolean.opBoolean","INTERSECT",EDGE,{"derivedFrom":[makeQuery(id+"F2.opShell","OFFSET_FACE",FACE,{"disambiguationData":[OSD([sQuery(id+"F0.wireOp",EDGE,"E4")])]}),makeQuery(id+"FnJFpvDc8nEjpgP_1.1.F5.opExtrude","SWEPT_FACE",FACE,{"disambiguationData":[OSD([sQuery(id+"F4.wireOp",EDGE,"E6.top")])]})]});
            var Q101;
            Q101=makeQuery(id+"FnJFpvDc8nEjpgP_1.2.F5.boolean.opBoolean","INTERSECT",EDGE,{"derivedFrom":[makeQuery(id+"F2.opShell","OFFSET_FACE",FACE,{"disambiguationData":[OSD([sQuery(id+"F0.wireOp",EDGE,"E4")])]}),makeQuery(id+"FnJFpvDc8nEjpgP_1.2.F5.opExtrude","SWEPT_FACE",FACE,{"disambiguationData":[OSD([sQuery(id+"F4.wireOp",EDGE,"E6.left")])]})]});
            var Q102;
            Q102=makeQuery(id+"FnJFpvDc8nEjpgP_1.2.F5.boolean.opBoolean","INTERSECT",EDGE,{"derivedFrom":[makeQuery(id+"F1.opRevolve","SWEPT_FACE",FACE,{"disambiguationData":[OSD([sQuery(id+"F0.wireOp",EDGE,"E4")])]}),makeQuery(id+"FnJFpvDc8nEjpgP_1.2.F5.opExtrude","SWEPT_FACE",FACE,{"disambiguationData":[OSD([sQuery(id+"F4.wireOp",EDGE,"E6.right")])]})]});
            var Q103;
            Q103=makeQuery(id+"FnJFpvDc8nEjpgP_1.2.F5.boolean.opBoolean","COPY",FACE,{"derivedFrom":makeQuery(id+"FnJFpvDc8nEjpgP_1.2.F5.opExtrude","SWEPT_FACE",FACE,{"disambiguationData":[OSD([sQuery(id+"F4.wireOp",EDGE,"E6.bottom")])]})});
            var Q104;
            Q104=makeQuery(id+"FnJFpvDc8nEjpgP_1.2.F5.boolean.opBoolean","COPY",FACE,{"derivedFrom":makeQuery(id+"FnJFpvDc8nEjpgP_1.2.F5.opExtrude","SWEPT_FACE",FACE,{"disambiguationData":[OSD([sQuery(id+"F4.wireOp",EDGE,"E6.top")])]})});
            var Q105;
            Q105=makeQuery(id+"FnJFpvDc8nEjpgP_1.2.F5.boolean.opBoolean","COPY",FACE,{"derivedFrom":makeQuery(id+"FnJFpvDc8nEjpgP_1.2.F5.opExtrude","SWEPT_FACE",FACE,{"disambiguationData":[OSD([sQuery(id+"F4.wireOp",EDGE,"E6.right")])]})});
            var Q106;
            Q106=makeQuery(id+"FnJFpvDc8nEjpgP_1.2.F5.boolean.opBoolean","COPY",FACE,{"derivedFrom":makeQuery(id+"FnJFpvDc8nEjpgP_1.2.F5.opExtrude","SWEPT_FACE",FACE,{"disambiguationData":[OSD([sQuery(id+"F4.wireOp",EDGE,"E7.filletArc")])]})});
            var Q107;
            Q107=makeQuery(id+"FnJFpvDc8nEjpgP_1.2.F5.boolean.opBoolean","COPY",FACE,{"derivedFrom":makeQuery(id+"FnJFpvDc8nEjpgP_1.2.F5.opExtrude","SWEPT_FACE",FACE,{"disambiguationData":[OSD([sQuery(id+"F4.wireOp",EDGE,"E10.filletArc")])]})});
            var Q108;
            Q108=makeQuery(id+"FnJFpvDc8nEjpgP_1.2.F5.boolean.opBoolean","INTERSECT",EDGE,{"derivedFrom":[makeQuery(id+"F1.opRevolve","SWEPT_FACE",FACE,{"disambiguationData":[OSD([sQuery(id+"F0.wireOp",EDGE,"E4")])]}),makeQuery(id+"FnJFpvDc8nEjpgP_1.2.F5.opExtrude","SWEPT_FACE",FACE,{"disambiguationData":[OSD([sQuery(id+"F4.wireOp",EDGE,"E6.bottom")])]})]});
            var Q109;
            Q109=makeQuery(id+"FnJFpvDc8nEjpgP_1.2.F5.boolean.opBoolean","INTERSECT",EDGE,{"derivedFrom":[makeQuery(id+"F1.opRevolve","SWEPT_FACE",FACE,{"disambiguationData":[OSD([sQuery(id+"F0.wireOp",EDGE,"E4")])]}),makeQuery(id+"FnJFpvDc8nEjpgP_1.2.F5.opExtrude","SWEPT_FACE",FACE,{"disambiguationData":[OSD([sQuery(id+"F4.wireOp",EDGE,"E6.top")])]})]});
            var Q110;
            Q110=makeQuery(id+"FnJFpvDc8nEjpgP_1.3.F5.boolean.opBoolean","INTERSECT",EDGE,{"derivedFrom":[makeQuery(id+"F2.opShell","OFFSET_FACE",FACE,{"disambiguationData":[OSD([sQuery(id+"F0.wireOp",EDGE,"E4")])]}),makeQuery(id+"FnJFpvDc8nEjpgP_1.3.F5.opExtrude","SWEPT_FACE",FACE,{"disambiguationData":[OSD([sQuery(id+"F4.wireOp",EDGE,"E6.left")])]})]});
            var Q111;
            Q111=makeQuery(id+"FnJFpvDc8nEjpgP_1.3.F5.boolean.opBoolean","INTERSECT",EDGE,{"derivedFrom":[makeQuery(id+"F2.opShell","OFFSET_FACE",FACE,{"disambiguationData":[OSD([sQuery(id+"F0.wireOp",EDGE,"E4")])]}),makeQuery(id+"FnJFpvDc8nEjpgP_1.3.F5.opExtrude","SWEPT_FACE",FACE,{"disambiguationData":[OSD([sQuery(id+"F4.wireOp",EDGE,"E6.right")])]})]});
            var Q112;
            Q112=makeQuery(id+"FnJFpvDc8nEjpgP_1.3.F5.boolean.opBoolean","COPY",EDGE,{"derivedFrom":makeQuery(id+"FnJFpvDc8nEjpgP_1.3.F5.opExtrude","SWEPT_EDGE",EDGE,{"disambiguationData":[OSD([sQuery(id+"F4.wireOp",EDGE,"E6.bottom"),sQuery(id+"F4.wireOp",EDGE,"E7.filletArc")])]})});
            var Q113;
            Q113=makeQuery(id+"FnJFpvDc8nEjpgP_1.3.F5.boolean.opBoolean","COPY",FACE,{"derivedFrom":makeQuery(id+"FnJFpvDc8nEjpgP_1.3.F5.opExtrude","SWEPT_FACE",FACE,{"disambiguationData":[OSD([sQuery(id+"F4.wireOp",EDGE,"E6.left")])]})});
            var Q114;
            Q114=makeQuery(id+"FnJFpvDc8nEjpgP_1.3.F5.boolean.opBoolean","COPY",FACE,{"derivedFrom":makeQuery(id+"FnJFpvDc8nEjpgP_1.3.F5.opExtrude","SWEPT_FACE",FACE,{"disambiguationData":[OSD([sQuery(id+"F4.wireOp",EDGE,"E7.filletArc")])]})});
            var Q115;
            Q115=makeQuery(id+"FnJFpvDc8nEjpgP_1.3.F5.boolean.opBoolean","COPY",FACE,{"derivedFrom":makeQuery(id+"FnJFpvDc8nEjpgP_1.3.F5.opExtrude","SWEPT_FACE",FACE,{"disambiguationData":[OSD([sQuery(id+"F4.wireOp",EDGE,"E8.filletArc")])]})});
            var Q116;
            Q116=makeQuery(id+"FnJFpvDc8nEjpgP_1.3.F5.boolean.opBoolean","COPY",EDGE,{"derivedFrom":makeQuery(id+"FnJFpvDc8nEjpgP_1.3.F5.opExtrude","SWEPT_EDGE",EDGE,{"disambiguationData":[OSD([sQuery(id+"F4.wireOp",EDGE,"E6.right"),sQuery(id+"F4.wireOp",EDGE,"E8.filletArc")])]})});
            var Q117;
            Q117=makeQuery(id+"FnJFpvDc8nEjpgP_1.3.F5.boolean.opBoolean","COPY",FACE,{"derivedFrom":makeQuery(id+"FnJFpvDc8nEjpgP_1.3.F5.opExtrude","SWEPT_FACE",FACE,{"disambiguationData":[OSD([sQuery(id+"F4.wireOp",EDGE,"E9.filletArc")])]})});
            var Q118;
            Q118=makeQuery(id+"FnJFpvDc8nEjpgP_1.3.F5.boolean.opBoolean","COPY",FACE,{"derivedFrom":makeQuery(id+"FnJFpvDc8nEjpgP_1.3.F5.opExtrude","SWEPT_FACE",FACE,{"disambiguationData":[OSD([sQuery(id+"F4.wireOp",EDGE,"E10.filletArc")])]})});
            var Q119;
            Q119=makeQuery(id+"FnJFpvDc8nEjpgP_1.3.F5.boolean.opBoolean","INTERSECT",EDGE,{"derivedFrom":[makeQuery(id+"F1.opRevolve","SWEPT_FACE",FACE,{"disambiguationData":[OSD([sQuery(id+"F0.wireOp",EDGE,"E4")])]}),makeQuery(id+"FnJFpvDc8nEjpgP_1.3.F5.opExtrude","SWEPT_FACE",FACE,{"disambiguationData":[OSD([sQuery(id+"F4.wireOp",EDGE,"E6.bottom")])]})]});
            var Q120;
            Q120=makeQuery(id+"FnJFpvDc8nEjpgP_1.3.F5.boolean.opBoolean","INTERSECT",EDGE,{"derivedFrom":[makeQuery(id+"F2.opShell","OFFSET_FACE",FACE,{"disambiguationData":[OSD([sQuery(id+"F0.wireOp",EDGE,"E4")])]}),makeQuery(id+"FnJFpvDc8nEjpgP_1.3.F5.opExtrude","SWEPT_FACE",FACE,{"disambiguationData":[OSD([sQuery(id+"F4.wireOp",EDGE,"E6.bottom")])]})]});
            var Q121;
            Q121=makeQuery(id+"FnJFpvDc8nEjpgP_1.3.F5.boolean.opBoolean","INTERSECT",EDGE,{"derivedFrom":[makeQuery(id+"F1.opRevolve","SWEPT_FACE",FACE,{"disambiguationData":[OSD([sQuery(id+"F0.wireOp",EDGE,"E4")])]}),makeQuery(id+"FnJFpvDc8nEjpgP_1.3.F5.opExtrude","SWEPT_FACE",FACE,{"disambiguationData":[OSD([sQuery(id+"F4.wireOp",EDGE,"E6.top")])]})]});
            var Q122;
            Q122=makeQuery(id+"FnJFpvDc8nEjpgP_1.4.F5.boolean.opBoolean","INTERSECT",EDGE,{"derivedFrom":[makeQuery(id+"F2.opShell","OFFSET_FACE",FACE,{"disambiguationData":[OSD([sQuery(id+"F0.wireOp",EDGE,"E4")])]}),makeQuery(id+"FnJFpvDc8nEjpgP_1.4.F5.opExtrude","SWEPT_FACE",FACE,{"disambiguationData":[OSD([sQuery(id+"F4.wireOp",EDGE,"E6.left")])]})]});
            var Q123;
            Q123=makeQuery(id+"FnJFpvDc8nEjpgP_1.4.F5.boolean.opBoolean","INTERSECT",EDGE,{"derivedFrom":[makeQuery(id+"F1.opRevolve","SWEPT_FACE",FACE,{"disambiguationData":[OSD([sQuery(id+"F0.wireOp",EDGE,"E4")])]}),makeQuery(id+"FnJFpvDc8nEjpgP_1.4.F5.opExtrude","SWEPT_FACE",FACE,{"disambiguationData":[OSD([sQuery(id+"F4.wireOp",EDGE,"E6.right")])]})]});
            var Q124;
            Q124=makeQuery(id+"FnJFpvDc8nEjpgP_1.4.F5.boolean.opBoolean","COPY",FACE,{"derivedFrom":makeQuery(id+"FnJFpvDc8nEjpgP_1.4.F5.opExtrude","SWEPT_FACE",FACE,{"disambiguationData":[OSD([sQuery(id+"F4.wireOp",EDGE,"E6.bottom")])]})});
            var Q125;
            Q125=makeQuery(id+"FnJFpvDc8nEjpgP_1.4.F5.boolean.opBoolean","COPY",FACE,{"derivedFrom":makeQuery(id+"FnJFpvDc8nEjpgP_1.4.F5.opExtrude","SWEPT_FACE",FACE,{"disambiguationData":[OSD([sQuery(id+"F4.wireOp",EDGE,"E6.right")])]})});
            var Q126;
            Q126=makeQuery(id+"FnJFpvDc8nEjpgP_1.4.F5.boolean.opBoolean","COPY",FACE,{"derivedFrom":makeQuery(id+"FnJFpvDc8nEjpgP_1.4.F5.opExtrude","SWEPT_FACE",FACE,{"disambiguationData":[OSD([sQuery(id+"F4.wireOp",EDGE,"E7.filletArc")])]})});
            var Q127;
            Q127=makeQuery(id+"FnJFpvDc8nEjpgP_1.4.F5.boolean.opBoolean","INTERSECT",EDGE,{"derivedFrom":[makeQuery(id+"F1.opRevolve","SWEPT_FACE",FACE,{"disambiguationData":[OSD([sQuery(id+"F0.wireOp",EDGE,"E4")])]}),makeQuery(id+"FnJFpvDc8nEjpgP_1.4.F5.opExtrude","SWEPT_FACE",FACE,{"disambiguationData":[OSD([sQuery(id+"F4.wireOp",EDGE,"E6.bottom")])]})]});
            var Q128;
            Q128=makeQuery(id+"FnJFpvDc8nEjpgP_1.4.F5.boolean.opBoolean","INTERSECT",EDGE,{"derivedFrom":[makeQuery(id+"F1.opRevolve","SWEPT_FACE",FACE,{"disambiguationData":[OSD([sQuery(id+"F0.wireOp",EDGE,"E4")])]}),makeQuery(id+"FnJFpvDc8nEjpgP_1.4.F5.opExtrude","SWEPT_FACE",FACE,{"disambiguationData":[OSD([sQuery(id+"F4.wireOp",EDGE,"E6.left")])]})]});
            var Q129;
            Q129=makeQuery(id+"FnJFpvDc8nEjpgP_1.5.F5.boolean.opBoolean","INTERSECT",EDGE,{"derivedFrom":[makeQuery(id+"F1.opRevolve","SWEPT_FACE",FACE,{"disambiguationData":[OSD([sQuery(id+"F0.wireOp",EDGE,"E4")])]}),makeQuery(id+"FnJFpvDc8nEjpgP_1.5.F5.opExtrude","SWEPT_FACE",FACE,{"disambiguationData":[OSD([sQuery(id+"F4.wireOp",EDGE,"E6.right")])]})]});
            var Q130;
            Q130=makeQuery(id+"FnJFpvDc8nEjpgP_1.5.F5.boolean.opBoolean","INTERSECT",EDGE,{"derivedFrom":[makeQuery(id+"F2.opShell","OFFSET_FACE",FACE,{"disambiguationData":[OSD([sQuery(id+"F0.wireOp",EDGE,"E4")])]}),makeQuery(id+"FnJFpvDc8nEjpgP_1.5.F5.opExtrude","SWEPT_FACE",FACE,{"disambiguationData":[OSD([sQuery(id+"F4.wireOp",EDGE,"E6.right")])]})]});
            var Q131;
            Q131=makeQuery(id+"FnJFpvDc8nEjpgP_1.5.F5.boolean.opBoolean","COPY",FACE,{"derivedFrom":makeQuery(id+"FnJFpvDc8nEjpgP_1.5.F5.opExtrude","SWEPT_FACE",FACE,{"disambiguationData":[OSD([sQuery(id+"F4.wireOp",EDGE,"E6.bottom")])]})});
            var Q132;
            Q132=makeQuery(id+"FnJFpvDc8nEjpgP_1.5.F5.boolean.opBoolean","COPY",FACE,{"derivedFrom":makeQuery(id+"FnJFpvDc8nEjpgP_1.5.F5.opExtrude","SWEPT_FACE",FACE,{"disambiguationData":[OSD([sQuery(id+"F4.wireOp",EDGE,"E6.right")])]})});
            var Q133;
            Q133=makeQuery(id+"FnJFpvDc8nEjpgP_1.5.F5.boolean.opBoolean","COPY",FACE,{"derivedFrom":makeQuery(id+"FnJFpvDc8nEjpgP_1.5.F5.opExtrude","SWEPT_FACE",FACE,{"disambiguationData":[OSD([sQuery(id+"F4.wireOp",EDGE,"E8.filletArc")])]})});
            var Q134;
            Q134=makeQuery(id+"FnJFpvDc8nEjpgP_1.5.F5.boolean.opBoolean","COPY",FACE,{"derivedFrom":makeQuery(id+"FnJFpvDc8nEjpgP_1.5.F5.opExtrude","SWEPT_FACE",FACE,{"disambiguationData":[OSD([sQuery(id+"F4.wireOp",EDGE,"E9.filletArc")])]})});
            var Q135;
            Q135=makeQuery(id+"FnJFpvDc8nEjpgP_1.5.F5.boolean.opBoolean","INTERSECT",EDGE,{"derivedFrom":[makeQuery(id+"F1.opRevolve","SWEPT_FACE",FACE,{"disambiguationData":[OSD([sQuery(id+"F0.wireOp",EDGE,"E4")])]}),makeQuery(id+"FnJFpvDc8nEjpgP_1.5.F5.opExtrude","SWEPT_FACE",FACE,{"disambiguationData":[OSD([sQuery(id+"F4.wireOp",EDGE,"E6.bottom")])]})]});
            var Q136;
            Q136=makeQuery(id+"FnJFpvDc8nEjpgP_1.5.F5.boolean.opBoolean","INTERSECT",EDGE,{"derivedFrom":[makeQuery(id+"F2.opShell","OFFSET_FACE",FACE,{"disambiguationData":[OSD([sQuery(id+"F0.wireOp",EDGE,"E4")])]}),makeQuery(id+"FnJFpvDc8nEjpgP_1.5.F5.opExtrude","SWEPT_FACE",FACE,{"disambiguationData":[OSD([sQuery(id+"F4.wireOp",EDGE,"E6.bottom")])]})]});
            var Q137;
            Q137=makeQuery(id+"FnJFpvDc8nEjpgP_1.5.F5.boolean.opBoolean","INTERSECT",EDGE,{"derivedFrom":[makeQuery(id+"F1.opRevolve","SWEPT_FACE",FACE,{"disambiguationData":[OSD([sQuery(id+"F0.wireOp",EDGE,"E4")])]}),makeQuery(id+"FnJFpvDc8nEjpgP_1.5.F5.opExtrude","SWEPT_FACE",FACE,{"disambiguationData":[OSD([sQuery(id+"F4.wireOp",EDGE,"E6.top")])]})]});
            var Q138;
            Q138=makeQuery(id+"FnJFpvDc8nEjpgP_1.5.F5.boolean.opBoolean","INTERSECT",EDGE,{"derivedFrom":[makeQuery(id+"F1.opRevolve","SWEPT_FACE",FACE,{"disambiguationData":[OSD([sQuery(id+"F0.wireOp",EDGE,"E4")])]}),makeQuery(id+"FnJFpvDc8nEjpgP_1.5.F5.opExtrude","SWEPT_FACE",FACE,{"disambiguationData":[OSD([sQuery(id+"F4.wireOp",EDGE,"E6.left")])]})]});
            var Q139;
            Q139=makeQuery(id+"FnJFpvDc8nEjpgP_1.6.F5.boolean.opBoolean","INTERSECT",EDGE,{"derivedFrom":[makeQuery(id+"F2.opShell","OFFSET_FACE",FACE,{"disambiguationData":[OSD([sQuery(id+"F0.wireOp",EDGE,"E4")])]}),makeQuery(id+"FnJFpvDc8nEjpgP_1.6.F5.opExtrude","SWEPT_FACE",FACE,{"disambiguationData":[OSD([sQuery(id+"F4.wireOp",EDGE,"E6.right")])]})]});
            var Q140;
            Q140=makeQuery(id+"FnJFpvDc8nEjpgP_1.6.F5.boolean.opBoolean","COPY",FACE,{"derivedFrom":makeQuery(id+"FnJFpvDc8nEjpgP_1.6.F5.opExtrude","SWEPT_FACE",FACE,{"disambiguationData":[OSD([sQuery(id+"F4.wireOp",EDGE,"E6.top")])]})});
            var Q141;
            Q141=makeQuery(id+"FnJFpvDc8nEjpgP_1.6.F5.boolean.opBoolean","COPY",EDGE,{"derivedFrom":makeQuery(id+"FnJFpvDc8nEjpgP_1.6.F5.opExtrude","SWEPT_EDGE",EDGE,{"disambiguationData":[OSD([sQuery(id+"F4.wireOp",EDGE,"E6.top"),sQuery(id+"F4.wireOp",EDGE,"E10.filletArc")])]})});
            var Q142;
            Q142=makeQuery(id+"FnJFpvDc8nEjpgP_1.6.F5.boolean.opBoolean","COPY",FACE,{"derivedFrom":makeQuery(id+"FnJFpvDc8nEjpgP_1.6.F5.opExtrude","SWEPT_FACE",FACE,{"disambiguationData":[OSD([sQuery(id+"F4.wireOp",EDGE,"E6.right")])]})});
            var Q143;
            Q143=makeQuery(id+"FnJFpvDc8nEjpgP_1.6.F5.boolean.opBoolean","COPY",FACE,{"derivedFrom":makeQuery(id+"FnJFpvDc8nEjpgP_1.6.F5.opExtrude","SWEPT_FACE",FACE,{"disambiguationData":[OSD([sQuery(id+"F4.wireOp",EDGE,"E8.filletArc")])]})});
            var Q144;
            Q144=makeQuery(id+"FnJFpvDc8nEjpgP_1.6.F5.boolean.opBoolean","COPY",EDGE,{"derivedFrom":makeQuery(id+"FnJFpvDc8nEjpgP_1.6.F5.opExtrude","SWEPT_EDGE",EDGE,{"disambiguationData":[OSD([sQuery(id+"F4.wireOp",EDGE,"E6.right"),sQuery(id+"F4.wireOp",EDGE,"E9.filletArc")])]})});
            var Q145;
            Q145=makeQuery(id+"FnJFpvDc8nEjpgP_1.6.F5.boolean.opBoolean","INTERSECT",EDGE,{"derivedFrom":[makeQuery(id+"F2.opShell","OFFSET_FACE",FACE,{"disambiguationData":[OSD([sQuery(id+"F0.wireOp",EDGE,"E4")])]}),makeQuery(id+"FnJFpvDc8nEjpgP_1.6.F5.opExtrude","SWEPT_FACE",FACE,{"disambiguationData":[OSD([sQuery(id+"F4.wireOp",EDGE,"E6.bottom")])]})]});
            var Q146;
            Q146=makeQuery(id+"FnJFpvDc8nEjpgP_1.6.F5.boolean.opBoolean","INTERSECT",EDGE,{"derivedFrom":[makeQuery(id+"F2.opShell","OFFSET_FACE",FACE,{"disambiguationData":[OSD([sQuery(id+"F0.wireOp",EDGE,"E4")])]}),makeQuery(id+"FnJFpvDc8nEjpgP_1.6.F5.opExtrude","SWEPT_FACE",FACE,{"disambiguationData":[OSD([sQuery(id+"F4.wireOp",EDGE,"E6.top")])]})]});
            var Q147;
            Q147=makeQuery(id+"FnJFpvDc8nEjpgP_1.6.F5.boolean.opBoolean","INTERSECT",EDGE,{"derivedFrom":[makeQuery(id+"F1.opRevolve","SWEPT_FACE",FACE,{"disambiguationData":[OSD([sQuery(id+"F0.wireOp",EDGE,"E4")])]}),makeQuery(id+"FnJFpvDc8nEjpgP_1.6.F5.opExtrude","SWEPT_FACE",FACE,{"disambiguationData":[OSD([sQuery(id+"F4.wireOp",EDGE,"E6.left")])]})]});
            var Q148;
            Q148=makeQuery(id+"FnJFpvDc8nEjpgP_1.1.F5.boolean.opBoolean","INTERSECT",EDGE,{"derivedFrom":[makeQuery(id+"F1.opRevolve","SWEPT_FACE",FACE,{"disambiguationData":[OSD([sQuery(id+"F0.wireOp",EDGE,"E4")])]}),makeQuery(id+"FnJFpvDc8nEjpgP_1.1.F5.opExtrude","SWEPT_FACE",FACE,{"disambiguationData":[OSD([sQuery(id+"F4.wireOp",EDGE,"E8.filletArc")])]})]});
            var Q149;
            Q149=makeQuery(id+"FnJFpvDc8nEjpgP_1.1.F5.boolean.opBoolean","INTERSECT",EDGE,{"derivedFrom":[makeQuery(id+"F2.opShell","OFFSET_FACE",FACE,{"disambiguationData":[OSD([sQuery(id+"F0.wireOp",EDGE,"E4")])]}),makeQuery(id+"FnJFpvDc8nEjpgP_1.1.F5.opExtrude","SWEPT_FACE",FACE,{"disambiguationData":[OSD([sQuery(id+"F4.wireOp",EDGE,"E8.filletArc")])]})]});
            var Q150;
            Q150=makeQuery(id+"FnJFpvDc8nEjpgP_1.1.F5.boolean.opBoolean","INTERSECT",EDGE,{"derivedFrom":[makeQuery(id+"F1.opRevolve","SWEPT_FACE",FACE,{"disambiguationData":[OSD([sQuery(id+"F0.wireOp",EDGE,"E4")])]}),makeQuery(id+"FnJFpvDc8nEjpgP_1.1.F5.opExtrude","SWEPT_FACE",FACE,{"disambiguationData":[OSD([sQuery(id+"F4.wireOp",EDGE,"E9.filletArc")])]})]});
            var Q151;
            Q151=makeQuery(id+"FnJFpvDc8nEjpgP_1.1.F5.boolean.opBoolean","INTERSECT",EDGE,{"derivedFrom":[makeQuery(id+"F2.opShell","OFFSET_FACE",FACE,{"disambiguationData":[OSD([sQuery(id+"F0.wireOp",EDGE,"E4")])]}),makeQuery(id+"FnJFpvDc8nEjpgP_1.1.F5.opExtrude","SWEPT_FACE",FACE,{"disambiguationData":[OSD([sQuery(id+"F4.wireOp",EDGE,"E10.filletArc")])]})]});
            var Q152;
            Q152=makeQuery(id+"FnJFpvDc8nEjpgP_1.2.F5.boolean.opBoolean","INTERSECT",EDGE,{"derivedFrom":[makeQuery(id+"F1.opRevolve","SWEPT_FACE",FACE,{"disambiguationData":[OSD([sQuery(id+"F0.wireOp",EDGE,"E4")])]}),makeQuery(id+"FnJFpvDc8nEjpgP_1.2.F5.opExtrude","SWEPT_FACE",FACE,{"disambiguationData":[OSD([sQuery(id+"F4.wireOp",EDGE,"E7.filletArc")])]})]});
            var Q153;
            Q153=makeQuery(id+"FnJFpvDc8nEjpgP_1.2.F5.boolean.opBoolean","INTERSECT",EDGE,{"derivedFrom":[makeQuery(id+"F1.opRevolve","SWEPT_FACE",FACE,{"disambiguationData":[OSD([sQuery(id+"F0.wireOp",EDGE,"E4")])]}),makeQuery(id+"FnJFpvDc8nEjpgP_1.2.F5.opExtrude","SWEPT_FACE",FACE,{"disambiguationData":[OSD([sQuery(id+"F4.wireOp",EDGE,"E8.filletArc")])]})]});
            var Q154;
            Q154=makeQuery(id+"FnJFpvDc8nEjpgP_1.2.F5.boolean.opBoolean","INTERSECT",EDGE,{"derivedFrom":[makeQuery(id+"F1.opRevolve","SWEPT_FACE",FACE,{"disambiguationData":[OSD([sQuery(id+"F0.wireOp",EDGE,"E4")])]}),makeQuery(id+"FnJFpvDc8nEjpgP_1.2.F5.opExtrude","SWEPT_FACE",FACE,{"disambiguationData":[OSD([sQuery(id+"F4.wireOp",EDGE,"E10.filletArc")])]})]});
            var Q155;
            Q155=makeQuery(id+"FnJFpvDc8nEjpgP_1.2.F5.boolean.opBoolean","INTERSECT",EDGE,{"derivedFrom":[makeQuery(id+"F2.opShell","OFFSET_FACE",FACE,{"disambiguationData":[OSD([sQuery(id+"F0.wireOp",EDGE,"E4")])]}),makeQuery(id+"FnJFpvDc8nEjpgP_1.2.F5.opExtrude","SWEPT_FACE",FACE,{"disambiguationData":[OSD([sQuery(id+"F4.wireOp",EDGE,"E10.filletArc")])]})]});
            var Q156;
            Q156=makeQuery(id+"FnJFpvDc8nEjpgP_1.3.F5.boolean.opBoolean","INTERSECT",EDGE,{"derivedFrom":[makeQuery(id+"F2.opShell","OFFSET_FACE",FACE,{"disambiguationData":[OSD([sQuery(id+"F0.wireOp",EDGE,"E4")])]}),makeQuery(id+"FnJFpvDc8nEjpgP_1.3.F5.opExtrude","SWEPT_FACE",FACE,{"disambiguationData":[OSD([sQuery(id+"F4.wireOp",EDGE,"E7.filletArc")])]})]});
            var Q157;
            Q157=makeQuery(id+"FnJFpvDc8nEjpgP_1.3.F5.boolean.opBoolean","INTERSECT",EDGE,{"derivedFrom":[makeQuery(id+"F2.opShell","OFFSET_FACE",FACE,{"disambiguationData":[OSD([sQuery(id+"F0.wireOp",EDGE,"E4")])]}),makeQuery(id+"FnJFpvDc8nEjpgP_1.3.F5.opExtrude","SWEPT_FACE",FACE,{"disambiguationData":[OSD([sQuery(id+"F4.wireOp",EDGE,"E9.filletArc")])]})]});
            var Q158;
            Q158=makeQuery(id+"FnJFpvDc8nEjpgP_1.3.F5.boolean.opBoolean","INTERSECT",EDGE,{"derivedFrom":[makeQuery(id+"F2.opShell","OFFSET_FACE",FACE,{"disambiguationData":[OSD([sQuery(id+"F0.wireOp",EDGE,"E4")])]}),makeQuery(id+"FnJFpvDc8nEjpgP_1.3.F5.opExtrude","SWEPT_FACE",FACE,{"disambiguationData":[OSD([sQuery(id+"F4.wireOp",EDGE,"E10.filletArc")])]})]});
            var Q159;
            Q159=makeQuery(id+"FnJFpvDc8nEjpgP_1.4.F5.boolean.opBoolean","INTERSECT",EDGE,{"derivedFrom":[makeQuery(id+"F2.opShell","OFFSET_FACE",FACE,{"disambiguationData":[OSD([sQuery(id+"F0.wireOp",EDGE,"E4")])]}),makeQuery(id+"FnJFpvDc8nEjpgP_1.4.F5.opExtrude","SWEPT_FACE",FACE,{"disambiguationData":[OSD([sQuery(id+"F4.wireOp",EDGE,"E9.filletArc")])]})]});
            var Q160;
            Q160=makeQuery(id+"FnJFpvDc8nEjpgP_1.4.F5.boolean.opBoolean","INTERSECT",EDGE,{"derivedFrom":[makeQuery(id+"F1.opRevolve","SWEPT_FACE",FACE,{"disambiguationData":[OSD([sQuery(id+"F0.wireOp",EDGE,"E4")])]}),makeQuery(id+"FnJFpvDc8nEjpgP_1.4.F5.opExtrude","SWEPT_FACE",FACE,{"disambiguationData":[OSD([sQuery(id+"F4.wireOp",EDGE,"E10.filletArc")])]})]});
            var Q161;
            Q161=makeQuery(id+"FnJFpvDc8nEjpgP_1.5.F5.boolean.opBoolean","INTERSECT",EDGE,{"derivedFrom":[makeQuery(id+"F2.opShell","OFFSET_FACE",FACE,{"disambiguationData":[OSD([sQuery(id+"F0.wireOp",EDGE,"E4")])]}),makeQuery(id+"FnJFpvDc8nEjpgP_1.5.F5.opExtrude","SWEPT_FACE",FACE,{"disambiguationData":[OSD([sQuery(id+"F4.wireOp",EDGE,"E8.filletArc")])]})]});
            var Q162;
            Q162=makeQuery(id+"FnJFpvDc8nEjpgP_1.5.F5.boolean.opBoolean","INTERSECT",EDGE,{"derivedFrom":[makeQuery(id+"F1.opRevolve","SWEPT_FACE",FACE,{"disambiguationData":[OSD([sQuery(id+"F0.wireOp",EDGE,"E4")])]}),makeQuery(id+"FnJFpvDc8nEjpgP_1.5.F5.opExtrude","SWEPT_FACE",FACE,{"disambiguationData":[OSD([sQuery(id+"F4.wireOp",EDGE,"E9.filletArc")])]})]});
            var Q163;
            Q163=makeQuery(id+"FnJFpvDc8nEjpgP_1.5.F5.boolean.opBoolean","INTERSECT",EDGE,{"derivedFrom":[makeQuery(id+"F2.opShell","OFFSET_FACE",FACE,{"disambiguationData":[OSD([sQuery(id+"F0.wireOp",EDGE,"E4")])]}),makeQuery(id+"FnJFpvDc8nEjpgP_1.5.F5.opExtrude","SWEPT_FACE",FACE,{"disambiguationData":[OSD([sQuery(id+"F4.wireOp",EDGE,"E10.filletArc")])]})]});
            var Q164;
            Q164=makeQuery(id+"FnJFpvDc8nEjpgP_1.6.F5.boolean.opBoolean","INTERSECT",EDGE,{"derivedFrom":[makeQuery(id+"F1.opRevolve","SWEPT_FACE",FACE,{"disambiguationData":[OSD([sQuery(id+"F0.wireOp",EDGE,"E4")])]}),makeQuery(id+"FnJFpvDc8nEjpgP_1.6.F5.opExtrude","SWEPT_FACE",FACE,{"disambiguationData":[OSD([sQuery(id+"F4.wireOp",EDGE,"E8.filletArc")])]})]});
            var Q165;
            Q165=makeQuery(id+"FnJFpvDc8nEjpgP_1.6.F5.boolean.opBoolean","INTERSECT",EDGE,{"derivedFrom":[makeQuery(id+"F1.opRevolve","SWEPT_FACE",FACE,{"disambiguationData":[OSD([sQuery(id+"F0.wireOp",EDGE,"E4")])]}),makeQuery(id+"FnJFpvDc8nEjpgP_1.6.F5.opExtrude","SWEPT_FACE",FACE,{"disambiguationData":[OSD([sQuery(id+"F4.wireOp",EDGE,"E9.filletArc")])]})]});
            var Q166;
            Q166=makeQuery(id+"FnJFpvDc8nEjpgP_1.6.F5.boolean.opBoolean","INTERSECT",EDGE,{"derivedFrom":[makeQuery(id+"F2.opShell","OFFSET_FACE",FACE,{"disambiguationData":[OSD([sQuery(id+"F0.wireOp",EDGE,"E4")])]}),makeQuery(id+"FnJFpvDc8nEjpgP_1.6.F5.opExtrude","SWEPT_FACE",FACE,{"disambiguationData":[OSD([sQuery(id+"F4.wireOp",EDGE,"E9.filletArc")])]})]});
            var Q167;
            Q167=makeQuery(id+"FnJFpvDc8nEjpgP_1.6.F5.boolean.opBoolean","INTERSECT",EDGE,{"derivedFrom":[makeQuery(id+"F1.opRevolve","SWEPT_FACE",FACE,{"disambiguationData":[OSD([sQuery(id+"F0.wireOp",EDGE,"E4")])]}),makeQuery(id+"FnJFpvDc8nEjpgP_1.6.F5.opExtrude","SWEPT_FACE",FACE,{"disambiguationData":[OSD([sQuery(id+"F4.wireOp",EDGE,"E10.filletArc")])]})]});
            var Q168;
            Q168=makeQuery(id+"F5.boolean.opBoolean","COPY",EDGE,{"derivedFrom":makeQuery(id+"F5.opExtrude","SWEPT_EDGE",EDGE,{"disambiguationData":[OSD([sQuery(id+"F4.wireOp",EDGE,"E6.bottom"),sQuery(id+"F4.wireOp",EDGE,"E8.filletArc")])]})});
            var Q169;
            Q169=makeQuery(id+"F5.boolean.opBoolean","COPY",EDGE,{"derivedFrom":makeQuery(id+"F5.opExtrude","SWEPT_EDGE",EDGE,{"disambiguationData":[OSD([sQuery(id+"F4.wireOp",EDGE,"E6.top"),sQuery(id+"F4.wireOp",EDGE,"E9.filletArc")])]})});
            var Q170;
            Q170=makeQuery(id+"F5.boolean.opBoolean","COPY",EDGE,{"derivedFrom":makeQuery(id+"F5.opExtrude","SWEPT_EDGE",EDGE,{"disambiguationData":[OSD([sQuery(id+"F4.wireOp",EDGE,"E6.left"),sQuery(id+"F4.wireOp",EDGE,"E10.filletArc")])]})});
            var Q171;
            Q171=makeQuery(id+"F5.boolean.opBoolean","INTERSECT",EDGE,{"derivedFrom":[makeQuery(id+"F1.opRevolve","SWEPT_FACE",FACE,{"disambiguationData":[OSD([sQuery(id+"F0.wireOp",EDGE,"E4")])]}),makeQuery(id+"F5.opExtrude","SWEPT_FACE",FACE,{"disambiguationData":[OSD([sQuery(id+"F4.wireOp",EDGE,"E9.filletArc")])]})]});
            var Q172;
            Q172=makeQuery(id+"F5.boolean.opBoolean","INTERSECT",EDGE,{"derivedFrom":[makeQuery(id+"F2.opShell","OFFSET_FACE",FACE,{"disambiguationData":[OSD([sQuery(id+"F0.wireOp",EDGE,"E4")])]}),makeQuery(id+"F5.opExtrude","SWEPT_FACE",FACE,{"disambiguationData":[OSD([sQuery(id+"F4.wireOp",EDGE,"E10.filletArc")])]})]});
            var Q173;
            Q173=makeQuery(id+"FnJFpvDc8nEjpgP_1.1.F5.boolean.opBoolean","COPY",EDGE,{"derivedFrom":makeQuery(id+"FnJFpvDc8nEjpgP_1.1.F5.opExtrude","SWEPT_EDGE",EDGE,{"disambiguationData":[OSD([sQuery(id+"F4.wireOp",EDGE,"E6.left"),sQuery(id+"F4.wireOp",EDGE,"E10.filletArc")])]})});
            var Q174;
            Q174=makeQuery(id+"FnJFpvDc8nEjpgP_1.1.F5.boolean.opBoolean","COPY",EDGE,{"derivedFrom":makeQuery(id+"FnJFpvDc8nEjpgP_1.1.F5.opExtrude","SWEPT_EDGE",EDGE,{"disambiguationData":[OSD([sQuery(id+"F4.wireOp",EDGE,"E6.right"),sQuery(id+"F4.wireOp",EDGE,"E9.filletArc")])]})});
            var Q175;
            Q175=makeQuery(id+"FnJFpvDc8nEjpgP_1.2.F5.boolean.opBoolean","INTERSECT",EDGE,{"derivedFrom":[makeQuery(id+"F2.opShell","OFFSET_FACE",FACE,{"disambiguationData":[OSD([sQuery(id+"F0.wireOp",EDGE,"E4")])]}),makeQuery(id+"FnJFpvDc8nEjpgP_1.2.F5.opExtrude","SWEPT_FACE",FACE,{"disambiguationData":[OSD([sQuery(id+"F4.wireOp",EDGE,"E6.right")])]})]});
            var Q176;
            Q176=makeQuery(id+"FnJFpvDc8nEjpgP_1.2.F5.boolean.opBoolean","COPY",EDGE,{"derivedFrom":makeQuery(id+"FnJFpvDc8nEjpgP_1.2.F5.opExtrude","SWEPT_EDGE",EDGE,{"disambiguationData":[OSD([sQuery(id+"F4.wireOp",EDGE,"E6.bottom"),sQuery(id+"F4.wireOp",EDGE,"E7.filletArc")])]})});
            var Q177;
            Q177=makeQuery(id+"FnJFpvDc8nEjpgP_1.2.F5.boolean.opBoolean","COPY",EDGE,{"derivedFrom":makeQuery(id+"FnJFpvDc8nEjpgP_1.2.F5.opExtrude","SWEPT_EDGE",EDGE,{"disambiguationData":[OSD([sQuery(id+"F4.wireOp",EDGE,"E6.bottom"),sQuery(id+"F4.wireOp",EDGE,"E8.filletArc")])]})});
            var Q178;
            Q178=makeQuery(id+"FnJFpvDc8nEjpgP_1.2.F5.boolean.opBoolean","COPY",EDGE,{"derivedFrom":makeQuery(id+"FnJFpvDc8nEjpgP_1.2.F5.opExtrude","SWEPT_EDGE",EDGE,{"disambiguationData":[OSD([sQuery(id+"F4.wireOp",EDGE,"E6.top"),sQuery(id+"F4.wireOp",EDGE,"E10.filletArc")])]})});
            var Q179;
            Q179=makeQuery(id+"FnJFpvDc8nEjpgP_1.2.F5.boolean.opBoolean","COPY",EDGE,{"derivedFrom":makeQuery(id+"FnJFpvDc8nEjpgP_1.2.F5.opExtrude","SWEPT_EDGE",EDGE,{"disambiguationData":[OSD([sQuery(id+"F4.wireOp",EDGE,"E6.top"),sQuery(id+"F4.wireOp",EDGE,"E9.filletArc")])]})});
            var Q180;
            Q180=makeQuery(id+"FnJFpvDc8nEjpgP_1.2.F5.boolean.opBoolean","COPY",EDGE,{"derivedFrom":makeQuery(id+"FnJFpvDc8nEjpgP_1.2.F5.opExtrude","SWEPT_EDGE",EDGE,{"disambiguationData":[OSD([sQuery(id+"F4.wireOp",EDGE,"E6.left"),sQuery(id+"F4.wireOp",EDGE,"E7.filletArc")])]})});
            var Q181;
            Q181=makeQuery(id+"FnJFpvDc8nEjpgP_1.2.F5.boolean.opBoolean","COPY",EDGE,{"derivedFrom":makeQuery(id+"FnJFpvDc8nEjpgP_1.2.F5.opExtrude","SWEPT_EDGE",EDGE,{"disambiguationData":[OSD([sQuery(id+"F4.wireOp",EDGE,"E6.left"),sQuery(id+"F4.wireOp",EDGE,"E10.filletArc")])]})});
            var Q182;
            Q182=makeQuery(id+"FnJFpvDc8nEjpgP_1.2.F5.boolean.opBoolean","COPY",FACE,{"derivedFrom":makeQuery(id+"FnJFpvDc8nEjpgP_1.2.F5.opExtrude","SWEPT_FACE",FACE,{"disambiguationData":[OSD([sQuery(id+"F4.wireOp",EDGE,"E8.filletArc")])]})});
            var Q183;
            Q183=makeQuery(id+"FnJFpvDc8nEjpgP_1.2.F5.boolean.opBoolean","COPY",EDGE,{"derivedFrom":makeQuery(id+"FnJFpvDc8nEjpgP_1.2.F5.opExtrude","SWEPT_EDGE",EDGE,{"disambiguationData":[OSD([sQuery(id+"F4.wireOp",EDGE,"E6.right"),sQuery(id+"F4.wireOp",EDGE,"E8.filletArc")])]})});
            var Q184;
            Q184=makeQuery(id+"FnJFpvDc8nEjpgP_1.2.F5.boolean.opBoolean","COPY",FACE,{"derivedFrom":makeQuery(id+"FnJFpvDc8nEjpgP_1.2.F5.opExtrude","SWEPT_FACE",FACE,{"disambiguationData":[OSD([sQuery(id+"F4.wireOp",EDGE,"E9.filletArc")])]})});
            var Q185;
            Q185=makeQuery(id+"FnJFpvDc8nEjpgP_1.2.F5.boolean.opBoolean","INTERSECT",EDGE,{"derivedFrom":[makeQuery(id+"F2.opShell","OFFSET_FACE",FACE,{"disambiguationData":[OSD([sQuery(id+"F0.wireOp",EDGE,"E4")])]}),makeQuery(id+"FnJFpvDc8nEjpgP_1.2.F5.opExtrude","SWEPT_FACE",FACE,{"disambiguationData":[OSD([sQuery(id+"F4.wireOp",EDGE,"E6.bottom")])]})]});
            var Q186;
            Q186=makeQuery(id+"FnJFpvDc8nEjpgP_1.2.F5.boolean.opBoolean","INTERSECT",EDGE,{"derivedFrom":[makeQuery(id+"F2.opShell","OFFSET_FACE",FACE,{"disambiguationData":[OSD([sQuery(id+"F0.wireOp",EDGE,"E4")])]}),makeQuery(id+"FnJFpvDc8nEjpgP_1.2.F5.opExtrude","SWEPT_FACE",FACE,{"disambiguationData":[OSD([sQuery(id+"F4.wireOp",EDGE,"E6.top")])]})]});
            var Q187;
            Q187=makeQuery(id+"FnJFpvDc8nEjpgP_1.3.F5.boolean.opBoolean","COPY",EDGE,{"derivedFrom":makeQuery(id+"FnJFpvDc8nEjpgP_1.3.F5.opExtrude","SWEPT_EDGE",EDGE,{"disambiguationData":[OSD([sQuery(id+"F4.wireOp",EDGE,"E6.bottom"),sQuery(id+"F4.wireOp",EDGE,"E8.filletArc")])]})});
            var Q188;
            Q188=makeQuery(id+"FnJFpvDc8nEjpgP_1.3.F5.boolean.opBoolean","COPY",FACE,{"derivedFrom":makeQuery(id+"FnJFpvDc8nEjpgP_1.3.F5.opExtrude","SWEPT_FACE",FACE,{"disambiguationData":[OSD([sQuery(id+"F4.wireOp",EDGE,"E6.top")])]})});
            var Q189;
            Q189=makeQuery(id+"FnJFpvDc8nEjpgP_1.3.F5.boolean.opBoolean","COPY",EDGE,{"derivedFrom":makeQuery(id+"FnJFpvDc8nEjpgP_1.3.F5.opExtrude","SWEPT_EDGE",EDGE,{"disambiguationData":[OSD([sQuery(id+"F4.wireOp",EDGE,"E6.top"),sQuery(id+"F4.wireOp",EDGE,"E10.filletArc")])]})});
            var Q190;
            Q190=makeQuery(id+"FnJFpvDc8nEjpgP_1.3.F5.boolean.opBoolean","COPY",EDGE,{"derivedFrom":makeQuery(id+"FnJFpvDc8nEjpgP_1.3.F5.opExtrude","SWEPT_EDGE",EDGE,{"disambiguationData":[OSD([sQuery(id+"F4.wireOp",EDGE,"E6.top"),sQuery(id+"F4.wireOp",EDGE,"E9.filletArc")])]})});
            var Q191;
            Q191=makeQuery(id+"FnJFpvDc8nEjpgP_1.3.F5.boolean.opBoolean","COPY",EDGE,{"derivedFrom":makeQuery(id+"FnJFpvDc8nEjpgP_1.3.F5.opExtrude","SWEPT_EDGE",EDGE,{"disambiguationData":[OSD([sQuery(id+"F4.wireOp",EDGE,"E6.left"),sQuery(id+"F4.wireOp",EDGE,"E7.filletArc")])]})});
            var Q192;
            Q192=makeQuery(id+"FnJFpvDc8nEjpgP_1.3.F5.boolean.opBoolean","COPY",EDGE,{"derivedFrom":makeQuery(id+"FnJFpvDc8nEjpgP_1.3.F5.opExtrude","SWEPT_EDGE",EDGE,{"disambiguationData":[OSD([sQuery(id+"F4.wireOp",EDGE,"E6.left"),sQuery(id+"F4.wireOp",EDGE,"E10.filletArc")])]})});
            var Q193;
            Q193=makeQuery(id+"FnJFpvDc8nEjpgP_1.3.F5.boolean.opBoolean","COPY",EDGE,{"derivedFrom":makeQuery(id+"FnJFpvDc8nEjpgP_1.3.F5.opExtrude","SWEPT_EDGE",EDGE,{"disambiguationData":[OSD([sQuery(id+"F4.wireOp",EDGE,"E6.right"),sQuery(id+"F4.wireOp",EDGE,"E9.filletArc")])]})});
            var Q194;
            Q194=makeQuery(id+"FnJFpvDc8nEjpgP_1.3.F5.boolean.opBoolean","INTERSECT",EDGE,{"derivedFrom":[makeQuery(id+"F2.opShell","OFFSET_FACE",FACE,{"disambiguationData":[OSD([sQuery(id+"F0.wireOp",EDGE,"E4")])]}),makeQuery(id+"FnJFpvDc8nEjpgP_1.3.F5.opExtrude","SWEPT_FACE",FACE,{"disambiguationData":[OSD([sQuery(id+"F4.wireOp",EDGE,"E6.top")])]})]});
            var Q195;
            Q195=makeQuery(id+"FnJFpvDc8nEjpgP_1.3.F5.boolean.opBoolean","INTERSECT",EDGE,{"derivedFrom":[makeQuery(id+"F1.opRevolve","SWEPT_FACE",FACE,{"disambiguationData":[OSD([sQuery(id+"F0.wireOp",EDGE,"E4")])]}),makeQuery(id+"FnJFpvDc8nEjpgP_1.3.F5.opExtrude","SWEPT_FACE",FACE,{"disambiguationData":[OSD([sQuery(id+"F4.wireOp",EDGE,"E6.left")])]})]});
            var Q196;
            Q196=makeQuery(id+"FnJFpvDc8nEjpgP_1.4.F5.boolean.opBoolean","COPY",EDGE,{"derivedFrom":makeQuery(id+"FnJFpvDc8nEjpgP_1.4.F5.opExtrude","SWEPT_EDGE",EDGE,{"disambiguationData":[OSD([sQuery(id+"F4.wireOp",EDGE,"E6.bottom"),sQuery(id+"F4.wireOp",EDGE,"E7.filletArc")])]})});
            var Q197;
            Q197=makeQuery(id+"FnJFpvDc8nEjpgP_1.4.F5.boolean.opBoolean","COPY",FACE,{"derivedFrom":makeQuery(id+"FnJFpvDc8nEjpgP_1.4.F5.opExtrude","SWEPT_FACE",FACE,{"disambiguationData":[OSD([sQuery(id+"F4.wireOp",EDGE,"E6.top")])]})});
            var Q198;
            Q198=makeQuery(id+"FnJFpvDc8nEjpgP_1.4.F5.boolean.opBoolean","COPY",EDGE,{"derivedFrom":makeQuery(id+"FnJFpvDc8nEjpgP_1.4.F5.opExtrude","SWEPT_EDGE",EDGE,{"disambiguationData":[OSD([sQuery(id+"F4.wireOp",EDGE,"E6.top"),sQuery(id+"F4.wireOp",EDGE,"E10.filletArc")])]})});
            var Q199;
            Q199=makeQuery(id+"FnJFpvDc8nEjpgP_1.4.F5.boolean.opBoolean","COPY",EDGE,{"derivedFrom":makeQuery(id+"FnJFpvDc8nEjpgP_1.4.F5.opExtrude","SWEPT_EDGE",EDGE,{"disambiguationData":[OSD([sQuery(id+"F4.wireOp",EDGE,"E6.top"),sQuery(id+"F4.wireOp",EDGE,"E9.filletArc")])]})});
            var Q200;
            Q200=makeQuery(id+"FnJFpvDc8nEjpgP_1.4.F5.boolean.opBoolean","COPY",EDGE,{"derivedFrom":makeQuery(id+"FnJFpvDc8nEjpgP_1.4.F5.opExtrude","SWEPT_EDGE",EDGE,{"disambiguationData":[OSD([sQuery(id+"F4.wireOp",EDGE,"E6.left"),sQuery(id+"F4.wireOp",EDGE,"E7.filletArc")])]})});
            var Q201;
            Q201=makeQuery(id+"FnJFpvDc8nEjpgP_1.4.F5.boolean.opBoolean","COPY",EDGE,{"derivedFrom":makeQuery(id+"FnJFpvDc8nEjpgP_1.4.F5.opExtrude","SWEPT_EDGE",EDGE,{"disambiguationData":[OSD([sQuery(id+"F4.wireOp",EDGE,"E6.left"),sQuery(id+"F4.wireOp",EDGE,"E10.filletArc")])]})});
            var Q202;
            Q202=makeQuery(id+"FnJFpvDc8nEjpgP_1.4.F5.boolean.opBoolean","COPY",FACE,{"derivedFrom":makeQuery(id+"FnJFpvDc8nEjpgP_1.4.F5.opExtrude","SWEPT_FACE",FACE,{"disambiguationData":[OSD([sQuery(id+"F4.wireOp",EDGE,"E8.filletArc")])]})});
            var Q203;
            Q203=makeQuery(id+"FnJFpvDc8nEjpgP_1.4.F5.boolean.opBoolean","COPY",EDGE,{"derivedFrom":makeQuery(id+"FnJFpvDc8nEjpgP_1.4.F5.opExtrude","SWEPT_EDGE",EDGE,{"disambiguationData":[OSD([sQuery(id+"F4.wireOp",EDGE,"E6.right"),sQuery(id+"F4.wireOp",EDGE,"E9.filletArc")])]})});
            var Q204;
            Q204=makeQuery(id+"FnJFpvDc8nEjpgP_1.4.F5.boolean.opBoolean","INTERSECT",EDGE,{"derivedFrom":[makeQuery(id+"F2.opShell","OFFSET_FACE",FACE,{"disambiguationData":[OSD([sQuery(id+"F0.wireOp",EDGE,"E4")])]}),makeQuery(id+"FnJFpvDc8nEjpgP_1.4.F5.opExtrude","SWEPT_FACE",FACE,{"disambiguationData":[OSD([sQuery(id+"F4.wireOp",EDGE,"E6.bottom")])]})]});
            var Q205;
            Q205=makeQuery(id+"FnJFpvDc8nEjpgP_1.4.F5.boolean.opBoolean","INTERSECT",EDGE,{"derivedFrom":[makeQuery(id+"F1.opRevolve","SWEPT_FACE",FACE,{"disambiguationData":[OSD([sQuery(id+"F0.wireOp",EDGE,"E4")])]}),makeQuery(id+"FnJFpvDc8nEjpgP_1.4.F5.opExtrude","SWEPT_FACE",FACE,{"disambiguationData":[OSD([sQuery(id+"F4.wireOp",EDGE,"E6.top")])]})]});
            var Q206;
            Q206=makeQuery(id+"FnJFpvDc8nEjpgP_1.4.F5.boolean.opBoolean","INTERSECT",EDGE,{"derivedFrom":[makeQuery(id+"F2.opShell","OFFSET_FACE",FACE,{"disambiguationData":[OSD([sQuery(id+"F0.wireOp",EDGE,"E4")])]}),makeQuery(id+"FnJFpvDc8nEjpgP_1.4.F5.opExtrude","SWEPT_FACE",FACE,{"disambiguationData":[OSD([sQuery(id+"F4.wireOp",EDGE,"E6.top")])]})]});
            var Q207;
            Q207=makeQuery(id+"FnJFpvDc8nEjpgP_1.5.F5.boolean.opBoolean","COPY",EDGE,{"derivedFrom":makeQuery(id+"FnJFpvDc8nEjpgP_1.5.F5.opExtrude","SWEPT_EDGE",EDGE,{"disambiguationData":[OSD([sQuery(id+"F4.wireOp",EDGE,"E6.bottom"),sQuery(id+"F4.wireOp",EDGE,"E7.filletArc")])]})});
            var Q208;
            Q208=makeQuery(id+"FnJFpvDc8nEjpgP_1.5.F5.boolean.opBoolean","COPY",EDGE,{"derivedFrom":makeQuery(id+"FnJFpvDc8nEjpgP_1.5.F5.opExtrude","SWEPT_EDGE",EDGE,{"disambiguationData":[OSD([sQuery(id+"F4.wireOp",EDGE,"E6.bottom"),sQuery(id+"F4.wireOp",EDGE,"E8.filletArc")])]})});
            var Q209;
            Q209=makeQuery(id+"FnJFpvDc8nEjpgP_1.5.F5.boolean.opBoolean","COPY",FACE,{"derivedFrom":makeQuery(id+"FnJFpvDc8nEjpgP_1.5.F5.opExtrude","SWEPT_FACE",FACE,{"disambiguationData":[OSD([sQuery(id+"F4.wireOp",EDGE,"E6.top")])]})});
            var Q210;
            Q210=makeQuery(id+"FnJFpvDc8nEjpgP_1.5.F5.boolean.opBoolean","COPY",EDGE,{"derivedFrom":makeQuery(id+"FnJFpvDc8nEjpgP_1.5.F5.opExtrude","SWEPT_EDGE",EDGE,{"disambiguationData":[OSD([sQuery(id+"F4.wireOp",EDGE,"E6.top"),sQuery(id+"F4.wireOp",EDGE,"E10.filletArc")])]})});
            var Q211;
            Q211=makeQuery(id+"FnJFpvDc8nEjpgP_1.5.F5.boolean.opBoolean","COPY",EDGE,{"derivedFrom":makeQuery(id+"FnJFpvDc8nEjpgP_1.5.F5.opExtrude","SWEPT_EDGE",EDGE,{"disambiguationData":[OSD([sQuery(id+"F4.wireOp",EDGE,"E6.top"),sQuery(id+"F4.wireOp",EDGE,"E9.filletArc")])]})});
            var Q212;
            Q212=makeQuery(id+"FnJFpvDc8nEjpgP_1.5.F5.boolean.opBoolean","COPY",FACE,{"derivedFrom":makeQuery(id+"FnJFpvDc8nEjpgP_1.5.F5.opExtrude","SWEPT_FACE",FACE,{"disambiguationData":[OSD([sQuery(id+"F4.wireOp",EDGE,"E7.filletArc")])]})});
            var Q213;
            Q213=makeQuery(id+"FnJFpvDc8nEjpgP_1.5.F5.boolean.opBoolean","COPY",EDGE,{"derivedFrom":makeQuery(id+"FnJFpvDc8nEjpgP_1.5.F5.opExtrude","SWEPT_EDGE",EDGE,{"disambiguationData":[OSD([sQuery(id+"F4.wireOp",EDGE,"E6.right"),sQuery(id+"F4.wireOp",EDGE,"E8.filletArc")])]})});
            var Q214;
            Q214=makeQuery(id+"FnJFpvDc8nEjpgP_1.5.F5.boolean.opBoolean","COPY",EDGE,{"derivedFrom":makeQuery(id+"FnJFpvDc8nEjpgP_1.5.F5.opExtrude","SWEPT_EDGE",EDGE,{"disambiguationData":[OSD([sQuery(id+"F4.wireOp",EDGE,"E6.right"),sQuery(id+"F4.wireOp",EDGE,"E9.filletArc")])]})});
            var Q215;
            Q215=makeQuery(id+"FnJFpvDc8nEjpgP_1.5.F5.boolean.opBoolean","COPY",FACE,{"derivedFrom":makeQuery(id+"FnJFpvDc8nEjpgP_1.5.F5.opExtrude","SWEPT_FACE",FACE,{"disambiguationData":[OSD([sQuery(id+"F4.wireOp",EDGE,"E10.filletArc")])]})});
            var Q216;
            Q216=makeQuery(id+"FnJFpvDc8nEjpgP_1.5.F5.boolean.opBoolean","INTERSECT",EDGE,{"derivedFrom":[makeQuery(id+"F2.opShell","OFFSET_FACE",FACE,{"disambiguationData":[OSD([sQuery(id+"F0.wireOp",EDGE,"E4")])]}),makeQuery(id+"FnJFpvDc8nEjpgP_1.5.F5.opExtrude","SWEPT_FACE",FACE,{"disambiguationData":[OSD([sQuery(id+"F4.wireOp",EDGE,"E6.top")])]})]});
            var Q217;
            Q217=makeQuery(id+"FnJFpvDc8nEjpgP_1.6.F5.boolean.opBoolean","COPY",EDGE,{"derivedFrom":makeQuery(id+"FnJFpvDc8nEjpgP_1.6.F5.opExtrude","SWEPT_EDGE",EDGE,{"disambiguationData":[OSD([sQuery(id+"F4.wireOp",EDGE,"E6.bottom"),sQuery(id+"F4.wireOp",EDGE,"E7.filletArc")])]})});
            var Q218;
            Q218=makeQuery(id+"FnJFpvDc8nEjpgP_1.6.F5.boolean.opBoolean","COPY",EDGE,{"derivedFrom":makeQuery(id+"FnJFpvDc8nEjpgP_1.6.F5.opExtrude","SWEPT_EDGE",EDGE,{"disambiguationData":[OSD([sQuery(id+"F4.wireOp",EDGE,"E6.bottom"),sQuery(id+"F4.wireOp",EDGE,"E8.filletArc")])]})});
            var Q219;
            Q219=makeQuery(id+"FnJFpvDc8nEjpgP_1.6.F5.boolean.opBoolean","COPY",EDGE,{"derivedFrom":makeQuery(id+"FnJFpvDc8nEjpgP_1.6.F5.opExtrude","SWEPT_EDGE",EDGE,{"disambiguationData":[OSD([sQuery(id+"F4.wireOp",EDGE,"E6.top"),sQuery(id+"F4.wireOp",EDGE,"E9.filletArc")])]})});
            var Q220;
            Q220=makeQuery(id+"FnJFpvDc8nEjpgP_1.6.F5.boolean.opBoolean","COPY",FACE,{"derivedFrom":makeQuery(id+"FnJFpvDc8nEjpgP_1.6.F5.opExtrude","SWEPT_FACE",FACE,{"disambiguationData":[OSD([sQuery(id+"F4.wireOp",EDGE,"E7.filletArc")])]})});
            var Q221;
            Q221=makeQuery(id+"FnJFpvDc8nEjpgP_1.6.F5.boolean.opBoolean","COPY",EDGE,{"derivedFrom":makeQuery(id+"FnJFpvDc8nEjpgP_1.6.F5.opExtrude","SWEPT_EDGE",EDGE,{"disambiguationData":[OSD([sQuery(id+"F4.wireOp",EDGE,"E6.right"),sQuery(id+"F4.wireOp",EDGE,"E8.filletArc")])]})});
            var Q222;
            Q222=makeQuery(id+"FnJFpvDc8nEjpgP_1.6.F5.boolean.opBoolean","COPY",FACE,{"derivedFrom":makeQuery(id+"FnJFpvDc8nEjpgP_1.6.F5.opExtrude","SWEPT_FACE",FACE,{"disambiguationData":[OSD([sQuery(id+"F4.wireOp",EDGE,"E10.filletArc")])]})});
            var Q223;
            Q223=makeQuery(id+"FnJFpvDc8nEjpgP_1.1.F5.boolean.opBoolean","INTERSECT",EDGE,{"derivedFrom":[makeQuery(id+"F2.opShell","OFFSET_FACE",FACE,{"disambiguationData":[OSD([sQuery(id+"F0.wireOp",EDGE,"E4")])]}),makeQuery(id+"FnJFpvDc8nEjpgP_1.1.F5.opExtrude","SWEPT_FACE",FACE,{"disambiguationData":[OSD([sQuery(id+"F4.wireOp",EDGE,"E7.filletArc")])]})]});
            var Q224;
            Q224=makeQuery(id+"FnJFpvDc8nEjpgP_1.1.F5.boolean.opBoolean","INTERSECT",EDGE,{"derivedFrom":[makeQuery(id+"F2.opShell","OFFSET_FACE",FACE,{"disambiguationData":[OSD([sQuery(id+"F0.wireOp",EDGE,"E4")])]}),makeQuery(id+"FnJFpvDc8nEjpgP_1.1.F5.opExtrude","SWEPT_FACE",FACE,{"disambiguationData":[OSD([sQuery(id+"F4.wireOp",EDGE,"E9.filletArc")])]})]});
            var Q225;
            Q225=makeQuery(id+"FnJFpvDc8nEjpgP_1.2.F5.boolean.opBoolean","INTERSECT",EDGE,{"derivedFrom":[makeQuery(id+"F2.opShell","OFFSET_FACE",FACE,{"disambiguationData":[OSD([sQuery(id+"F0.wireOp",EDGE,"E4")])]}),makeQuery(id+"FnJFpvDc8nEjpgP_1.2.F5.opExtrude","SWEPT_FACE",FACE,{"disambiguationData":[OSD([sQuery(id+"F4.wireOp",EDGE,"E7.filletArc")])]})]});
            var Q226;
            Q226=makeQuery(id+"FnJFpvDc8nEjpgP_1.2.F5.boolean.opBoolean","INTERSECT",EDGE,{"derivedFrom":[makeQuery(id+"F2.opShell","OFFSET_FACE",FACE,{"disambiguationData":[OSD([sQuery(id+"F0.wireOp",EDGE,"E4")])]}),makeQuery(id+"FnJFpvDc8nEjpgP_1.2.F5.opExtrude","SWEPT_FACE",FACE,{"disambiguationData":[OSD([sQuery(id+"F4.wireOp",EDGE,"E8.filletArc")])]})]});
            var Q227;
            Q227=makeQuery(id+"FnJFpvDc8nEjpgP_1.2.F5.boolean.opBoolean","INTERSECT",EDGE,{"derivedFrom":[makeQuery(id+"F1.opRevolve","SWEPT_FACE",FACE,{"disambiguationData":[OSD([sQuery(id+"F0.wireOp",EDGE,"E4")])]}),makeQuery(id+"FnJFpvDc8nEjpgP_1.2.F5.opExtrude","SWEPT_FACE",FACE,{"disambiguationData":[OSD([sQuery(id+"F4.wireOp",EDGE,"E9.filletArc")])]})]});
            var Q228;
            Q228=makeQuery(id+"FnJFpvDc8nEjpgP_1.2.F5.boolean.opBoolean","INTERSECT",EDGE,{"derivedFrom":[makeQuery(id+"F2.opShell","OFFSET_FACE",FACE,{"disambiguationData":[OSD([sQuery(id+"F0.wireOp",EDGE,"E4")])]}),makeQuery(id+"FnJFpvDc8nEjpgP_1.2.F5.opExtrude","SWEPT_FACE",FACE,{"disambiguationData":[OSD([sQuery(id+"F4.wireOp",EDGE,"E9.filletArc")])]})]});
            var Q229;
            Q229=makeQuery(id+"FnJFpvDc8nEjpgP_1.3.F5.boolean.opBoolean","INTERSECT",EDGE,{"derivedFrom":[makeQuery(id+"F1.opRevolve","SWEPT_FACE",FACE,{"disambiguationData":[OSD([sQuery(id+"F0.wireOp",EDGE,"E4")])]}),makeQuery(id+"FnJFpvDc8nEjpgP_1.3.F5.opExtrude","SWEPT_FACE",FACE,{"disambiguationData":[OSD([sQuery(id+"F4.wireOp",EDGE,"E8.filletArc")])]})]});
            var Q230;
            Q230=makeQuery(id+"FnJFpvDc8nEjpgP_1.3.F5.boolean.opBoolean","INTERSECT",EDGE,{"derivedFrom":[makeQuery(id+"F2.opShell","OFFSET_FACE",FACE,{"disambiguationData":[OSD([sQuery(id+"F0.wireOp",EDGE,"E4")])]}),makeQuery(id+"FnJFpvDc8nEjpgP_1.3.F5.opExtrude","SWEPT_FACE",FACE,{"disambiguationData":[OSD([sQuery(id+"F4.wireOp",EDGE,"E8.filletArc")])]})]});
            var Q231;
            Q231=makeQuery(id+"FnJFpvDc8nEjpgP_1.3.F5.boolean.opBoolean","INTERSECT",EDGE,{"derivedFrom":[makeQuery(id+"F1.opRevolve","SWEPT_FACE",FACE,{"disambiguationData":[OSD([sQuery(id+"F0.wireOp",EDGE,"E4")])]}),makeQuery(id+"FnJFpvDc8nEjpgP_1.3.F5.opExtrude","SWEPT_FACE",FACE,{"disambiguationData":[OSD([sQuery(id+"F4.wireOp",EDGE,"E9.filletArc")])]})]});
            var Q232;
            Q232=makeQuery(id+"FnJFpvDc8nEjpgP_1.3.F5.boolean.opBoolean","INTERSECT",EDGE,{"derivedFrom":[makeQuery(id+"F1.opRevolve","SWEPT_FACE",FACE,{"disambiguationData":[OSD([sQuery(id+"F0.wireOp",EDGE,"E4")])]}),makeQuery(id+"FnJFpvDc8nEjpgP_1.3.F5.opExtrude","SWEPT_FACE",FACE,{"disambiguationData":[OSD([sQuery(id+"F4.wireOp",EDGE,"E10.filletArc")])]})]});
            var Q233;
            Q233=makeQuery(id+"FnJFpvDc8nEjpgP_1.4.F5.boolean.opBoolean","INTERSECT",EDGE,{"derivedFrom":[makeQuery(id+"F1.opRevolve","SWEPT_FACE",FACE,{"disambiguationData":[OSD([sQuery(id+"F0.wireOp",EDGE,"E4")])]}),makeQuery(id+"FnJFpvDc8nEjpgP_1.4.F5.opExtrude","SWEPT_FACE",FACE,{"disambiguationData":[OSD([sQuery(id+"F4.wireOp",EDGE,"E7.filletArc")])]})]});
            var Q234;
            Q234=makeQuery(id+"FnJFpvDc8nEjpgP_1.4.F5.boolean.opBoolean","INTERSECT",EDGE,{"derivedFrom":[makeQuery(id+"F2.opShell","OFFSET_FACE",FACE,{"disambiguationData":[OSD([sQuery(id+"F0.wireOp",EDGE,"E4")])]}),makeQuery(id+"FnJFpvDc8nEjpgP_1.4.F5.opExtrude","SWEPT_FACE",FACE,{"disambiguationData":[OSD([sQuery(id+"F4.wireOp",EDGE,"E7.filletArc")])]})]});
            var Q235;
            Q235=makeQuery(id+"FnJFpvDc8nEjpgP_1.4.F5.boolean.opBoolean","INTERSECT",EDGE,{"derivedFrom":[makeQuery(id+"F1.opRevolve","SWEPT_FACE",FACE,{"disambiguationData":[OSD([sQuery(id+"F0.wireOp",EDGE,"E4")])]}),makeQuery(id+"FnJFpvDc8nEjpgP_1.4.F5.opExtrude","SWEPT_FACE",FACE,{"disambiguationData":[OSD([sQuery(id+"F4.wireOp",EDGE,"E8.filletArc")])]})]});
            var Q236;
            Q236=makeQuery(id+"FnJFpvDc8nEjpgP_1.4.F5.boolean.opBoolean","INTERSECT",EDGE,{"derivedFrom":[makeQuery(id+"F2.opShell","OFFSET_FACE",FACE,{"disambiguationData":[OSD([sQuery(id+"F0.wireOp",EDGE,"E4")])]}),makeQuery(id+"FnJFpvDc8nEjpgP_1.4.F5.opExtrude","SWEPT_FACE",FACE,{"disambiguationData":[OSD([sQuery(id+"F4.wireOp",EDGE,"E8.filletArc")])]})]});
            var Q237;
            Q237=makeQuery(id+"FnJFpvDc8nEjpgP_1.4.F5.boolean.opBoolean","INTERSECT",EDGE,{"derivedFrom":[makeQuery(id+"F1.opRevolve","SWEPT_FACE",FACE,{"disambiguationData":[OSD([sQuery(id+"F0.wireOp",EDGE,"E4")])]}),makeQuery(id+"FnJFpvDc8nEjpgP_1.4.F5.opExtrude","SWEPT_FACE",FACE,{"disambiguationData":[OSD([sQuery(id+"F4.wireOp",EDGE,"E9.filletArc")])]})]});
            var Q238;
            Q238=makeQuery(id+"FnJFpvDc8nEjpgP_1.5.F5.boolean.opBoolean","INTERSECT",EDGE,{"derivedFrom":[makeQuery(id+"F2.opShell","OFFSET_FACE",FACE,{"disambiguationData":[OSD([sQuery(id+"F0.wireOp",EDGE,"E4")])]}),makeQuery(id+"FnJFpvDc8nEjpgP_1.5.F5.opExtrude","SWEPT_FACE",FACE,{"disambiguationData":[OSD([sQuery(id+"F4.wireOp",EDGE,"E7.filletArc")])]})]});
            var Q239;
            Q239=makeQuery(id+"FnJFpvDc8nEjpgP_1.5.F5.boolean.opBoolean","INTERSECT",EDGE,{"derivedFrom":[makeQuery(id+"F1.opRevolve","SWEPT_FACE",FACE,{"disambiguationData":[OSD([sQuery(id+"F0.wireOp",EDGE,"E4")])]}),makeQuery(id+"FnJFpvDc8nEjpgP_1.5.F5.opExtrude","SWEPT_FACE",FACE,{"disambiguationData":[OSD([sQuery(id+"F4.wireOp",EDGE,"E8.filletArc")])]})]});
            var Q240;
            Q240=makeQuery(id+"FnJFpvDc8nEjpgP_1.5.F5.boolean.opBoolean","INTERSECT",EDGE,{"derivedFrom":[makeQuery(id+"F2.opShell","OFFSET_FACE",FACE,{"disambiguationData":[OSD([sQuery(id+"F0.wireOp",EDGE,"E4")])]}),makeQuery(id+"FnJFpvDc8nEjpgP_1.5.F5.opExtrude","SWEPT_FACE",FACE,{"disambiguationData":[OSD([sQuery(id+"F4.wireOp",EDGE,"E9.filletArc")])]})]});
            var Q241;
            Q241=makeQuery(id+"FnJFpvDc8nEjpgP_1.6.F5.boolean.opBoolean","INTERSECT",EDGE,{"derivedFrom":[makeQuery(id+"F1.opRevolve","SWEPT_FACE",FACE,{"disambiguationData":[OSD([sQuery(id+"F0.wireOp",EDGE,"E4")])]}),makeQuery(id+"FnJFpvDc8nEjpgP_1.6.F5.opExtrude","SWEPT_FACE",FACE,{"disambiguationData":[OSD([sQuery(id+"F4.wireOp",EDGE,"E7.filletArc")])]})]});
            var Q242;
            Q242=makeQuery(id+"FnJFpvDc8nEjpgP_1.6.F5.boolean.opBoolean","INTERSECT",EDGE,{"derivedFrom":[makeQuery(id+"F2.opShell","OFFSET_FACE",FACE,{"disambiguationData":[OSD([sQuery(id+"F0.wireOp",EDGE,"E4")])]}),makeQuery(id+"FnJFpvDc8nEjpgP_1.6.F5.opExtrude","SWEPT_FACE",FACE,{"disambiguationData":[OSD([sQuery(id+"F4.wireOp",EDGE,"E8.filletArc")])]})]});
            var Q243;
            Q243=makeQuery(id+"FnJFpvDc8nEjpgP_1.6.F5.boolean.opBoolean","INTERSECT",EDGE,{"derivedFrom":[makeQuery(id+"F2.opShell","OFFSET_FACE",FACE,{"disambiguationData":[OSD([sQuery(id+"F0.wireOp",EDGE,"E4")])]}),makeQuery(id+"FnJFpvDc8nEjpgP_1.6.F5.opExtrude","SWEPT_FACE",FACE,{"disambiguationData":[OSD([sQuery(id+"F4.wireOp",EDGE,"E10.filletArc")])]})]});
            var Q244;
            Q244=makeQuery(id+"F5.boolean.opBoolean","COPY",EDGE,{"derivedFrom":makeQuery(id+"F5.opExtrude","SWEPT_EDGE",EDGE,{"disambiguationData":[OSD([sQuery(id+"F4.wireOp",EDGE,"E6.right"),sQuery(id+"F4.wireOp",EDGE,"E9.filletArc")])]})});
            var Q245;
            Q245=makeQuery(id+"FnJFpvDc8nEjpgP_1.2.F5.boolean.opBoolean","COPY",EDGE,{"derivedFrom":makeQuery(id+"FnJFpvDc8nEjpgP_1.2.F5.opExtrude","SWEPT_EDGE",EDGE,{"disambiguationData":[OSD([sQuery(id+"F4.wireOp",EDGE,"E6.right"),sQuery(id+"F4.wireOp",EDGE,"E9.filletArc")])]})});
            var Q246;
            Q246=makeQuery(id+"FnJFpvDc8nEjpgP_1.4.F5.boolean.opBoolean","COPY",EDGE,{"derivedFrom":makeQuery(id+"FnJFpvDc8nEjpgP_1.4.F5.opExtrude","SWEPT_EDGE",EDGE,{"disambiguationData":[OSD([sQuery(id+"F4.wireOp",EDGE,"E6.bottom"),sQuery(id+"F4.wireOp",EDGE,"E8.filletArc")])]})});
            var Q247;
            Q247=makeQuery(id+"FnJFpvDc8nEjpgP_1.4.F5.boolean.opBoolean","COPY",EDGE,{"derivedFrom":makeQuery(id+"FnJFpvDc8nEjpgP_1.4.F5.opExtrude","SWEPT_EDGE",EDGE,{"disambiguationData":[OSD([sQuery(id+"F4.wireOp",EDGE,"E6.right"),sQuery(id+"F4.wireOp",EDGE,"E8.filletArc")])]})});
            var Q248;
            Q248=makeQuery(id+"FnJFpvDc8nEjpgP_1.5.F5.boolean.opBoolean","COPY",EDGE,{"derivedFrom":makeQuery(id+"FnJFpvDc8nEjpgP_1.5.F5.opExtrude","SWEPT_EDGE",EDGE,{"disambiguationData":[OSD([sQuery(id+"F4.wireOp",EDGE,"E6.left"),sQuery(id+"F4.wireOp",EDGE,"E7.filletArc")])]})});
            var Q249;
            Q249=makeQuery(id+"FnJFpvDc8nEjpgP_1.5.F5.boolean.opBoolean","COPY",EDGE,{"derivedFrom":makeQuery(id+"FnJFpvDc8nEjpgP_1.5.F5.opExtrude","SWEPT_EDGE",EDGE,{"disambiguationData":[OSD([sQuery(id+"F4.wireOp",EDGE,"E6.left"),sQuery(id+"F4.wireOp",EDGE,"E10.filletArc")])]})});
            var Q250;
            Q250=makeQuery(id+"FnJFpvDc8nEjpgP_1.6.F5.boolean.opBoolean","COPY",EDGE,{"derivedFrom":makeQuery(id+"FnJFpvDc8nEjpgP_1.6.F5.opExtrude","SWEPT_EDGE",EDGE,{"disambiguationData":[OSD([sQuery(id+"F4.wireOp",EDGE,"E6.left"),sQuery(id+"F4.wireOp",EDGE,"E7.filletArc")])]})});
            var Q251;
            Q251=makeQuery(id+"FnJFpvDc8nEjpgP_1.6.F5.boolean.opBoolean","COPY",EDGE,{"derivedFrom":makeQuery(id+"FnJFpvDc8nEjpgP_1.6.F5.opExtrude","SWEPT_EDGE",EDGE,{"disambiguationData":[OSD([sQuery(id+"F4.wireOp",EDGE,"E6.left"),sQuery(id+"F4.wireOp",EDGE,"E10.filletArc")])]})});
            var Q252;
            Q252=makeQuery(id+"FnJFpvDc8nEjpgP_1.3.F5.boolean.opBoolean","INTERSECT",EDGE,{"derivedFrom":[makeQuery(id+"F1.opRevolve","SWEPT_FACE",FACE,{"disambiguationData":[OSD([sQuery(id+"F0.wireOp",EDGE,"E4")])]}),makeQuery(id+"FnJFpvDc8nEjpgP_1.3.F5.opExtrude","SWEPT_FACE",FACE,{"disambiguationData":[OSD([sQuery(id+"F4.wireOp",EDGE,"E7.filletArc")])]})]});
            var Q253;
            Q253=makeQuery(id+"FnJFpvDc8nEjpgP_1.5.F5.boolean.opBoolean","INTERSECT",EDGE,{"derivedFrom":[makeQuery(id+"F1.opRevolve","SWEPT_FACE",FACE,{"disambiguationData":[OSD([sQuery(id+"F0.wireOp",EDGE,"E4")])]}),makeQuery(id+"FnJFpvDc8nEjpgP_1.5.F5.opExtrude","SWEPT_FACE",FACE,{"disambiguationData":[OSD([sQuery(id+"F4.wireOp",EDGE,"E7.filletArc")])]})]});
            var Q254;
            Q254=makeQuery(id+"FnJFpvDc8nEjpgP_1.5.F5.boolean.opBoolean","INTERSECT",EDGE,{"derivedFrom":[makeQuery(id+"F1.opRevolve","SWEPT_FACE",FACE,{"disambiguationData":[OSD([sQuery(id+"F0.wireOp",EDGE,"E4")])]}),makeQuery(id+"FnJFpvDc8nEjpgP_1.5.F5.opExtrude","SWEPT_FACE",FACE,{"disambiguationData":[OSD([sQuery(id+"F4.wireOp",EDGE,"E10.filletArc")])]})]});
            var Q255;
            Q255=makeQuery(id+"FnJFpvDc8nEjpgP_1.6.F5.boolean.opBoolean","INTERSECT",EDGE,{"derivedFrom":[makeQuery(id+"F2.opShell","OFFSET_FACE",FACE,{"disambiguationData":[OSD([sQuery(id+"F0.wireOp",EDGE,"E4")])]}),makeQuery(id+"FnJFpvDc8nEjpgP_1.6.F5.opExtrude","SWEPT_FACE",FACE,{"disambiguationData":[OSD([sQuery(id+"F4.wireOp",EDGE,"E7.filletArc")])]})]});
            fillet(context, id + "F6", {"entities" : qUnion([Q0, Q1, Q2, Q3, Q4, Q5, Q6, Q7, Q8, Q9, Q10, Q11, Q12, Q13, Q14, Q15, Q16, Q17, Q18, Q19, Q20, Q21, Q22, Q23, Q24, Q25, Q26, Q27, Q28, Q29, Q30, Q31, Q32, Q33, Q34, Q35, Q36, Q37, Q38, Q39, Q40, Q41, Q42, Q43, Q44, Q45, Q46, Q47, Q48, Q49, Q50, Q51, Q52, Q53, Q54, Q55, Q56, Q57, Q58, Q59, Q60, Q61, Q62, Q63, Q64, Q65, Q66, Q67, Q68, Q69, Q70, Q71, Q72, Q73, Q74, Q75, Q76, Q77, Q78, Q79, Q80, Q81, Q82, Q83, Q84, Q85, Q86, Q87, Q88, Q89, Q90, Q91, Q92, Q93, Q94, Q95, Q96, Q97, Q98, Q99, Q100, Q101, Q102, Q103, Q104, Q105, Q106, Q107, Q108, Q109, Q110, Q111, Q112, Q113, Q114, Q115, Q116, Q117, Q118, Q119, Q120, Q121, Q122, Q123, Q124, Q125, Q126, Q127, Q128, Q129, Q130, Q131, Q132, Q133, Q134, Q135, Q136, Q137, Q138, Q139, Q140, Q141, Q142, Q143, Q144, Q145, Q146, Q147, Q148, Q149, Q150, Q151, Q152, Q153, Q154, Q155, Q156, Q157, Q158, Q159, Q160, Q161, Q162, Q163, Q164, Q165, Q166, Q167, Q168, Q169, Q170, Q171, Q172, Q173, Q174, Q175, Q176, Q177, Q178, Q179, Q180, Q181, Q182, Q183, Q184, Q185, Q186, Q187, Q188, Q189, Q190, Q191, Q192, Q193, Q194, Q195, Q196, Q197, Q198, Q199, Q200, Q201, Q202, Q203, Q204, Q205, Q206, Q207, Q208, Q209, Q210, Q211, Q212, Q213, Q214, Q215, Q216, Q217, Q218, Q219, Q220, Q221, Q222, Q223, Q224, Q225, Q226, Q227, Q228, Q229, Q230, Q231, Q232, Q233, Q234, Q235, Q236, Q237, Q238, Q239, Q240, Q241, Q242, Q243, Q244, Q245, Q246, Q247, Q248, Q249, Q250, Q251, Q252, Q253, Q254, Q255]), "radius" : 0.15 * mm, "tangentPropagation" : true, "allowEdgeOverflow" : false});
        }
    });
